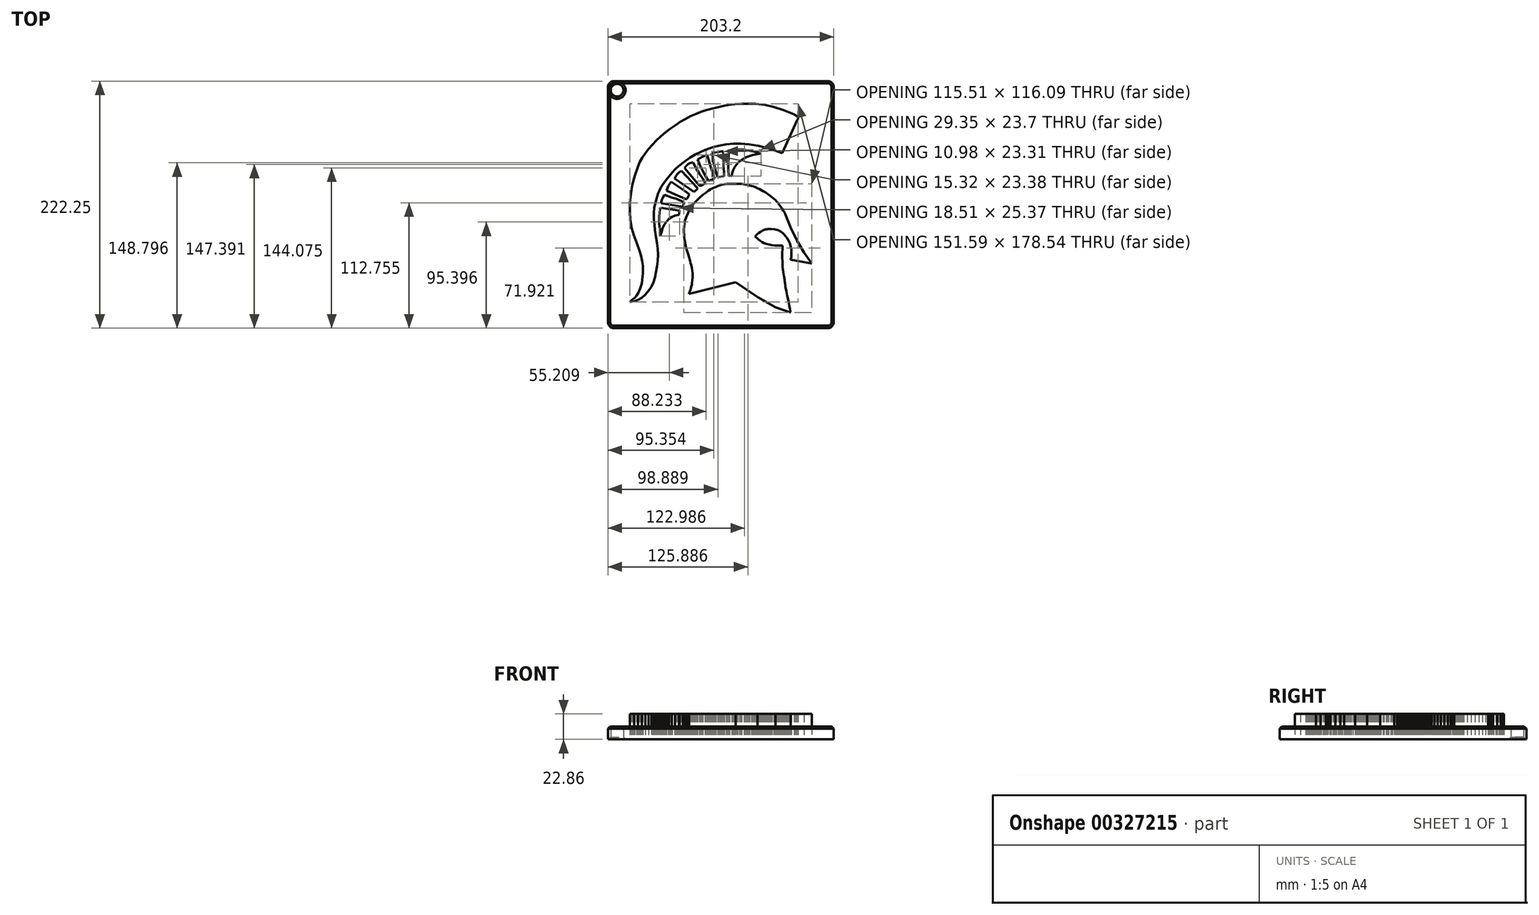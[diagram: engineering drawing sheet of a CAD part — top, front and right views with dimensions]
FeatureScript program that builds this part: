
annotation { "Feature Type Name" : "Feature", "Feature Type Description" : "" }
export const myFeature = defineFeature(function(context is Context, id is Id, definition is map)
    precondition{}
    {
        {
            var Q0;
            Q0=qCreatedBy(makeId("Top.planeOp"),FACE);
            var sketch = newSketch(context, id + "F0", { "sketchPlane" : qUnion([Q0])});
            skLineSegment(sketch, "E0", {"start": v(-81.82, -84.47) * mm, "end": v(-80.11, -82.47) * mm});
            skLineSegment(sketch, "E1", {"start": v(-80.11, -82.47) * mm, "end": v(-79.76, -82.32) * mm});
            skLineSegment(sketch, "E2", {"start": v(-79.76, -82.32) * mm, "end": v(-78.83, -81.76) * mm});
            skLineSegment(sketch, "E3", {"start": v(-78.83, -81.76) * mm, "end": v(-77.48, -80.64) * mm});
            skLineSegment(sketch, "E4", {"start": v(-77.48, -80.64) * mm, "end": v(-75.88, -78.83) * mm});
            skLineSegment(sketch, "E5", {"start": v(-75.88, -78.83) * mm, "end": v(-74.2, -76.16) * mm});
            skLineSegment(sketch, "E6", {"start": v(-74.2, -76.16) * mm, "end": v(-72.61, -72.5) * mm});
            skLineSegment(sketch, "E7", {"start": v(-72.61, -72.5) * mm, "end": v(-71.28, -67.7) * mm});
            skLineSegment(sketch, "E8", {"start": v(-71.28, -67.7) * mm, "end": v(-70.36, -61.6) * mm});
            skLineSegment(sketch, "E9", {"start": v(-70.36, -61.6) * mm, "end": v(-70.11, -58.43) * mm});
            skLineSegment(sketch, "E10", {"start": v(-70.11, -58.43) * mm, "end": v(-70.03, -55.21) * mm});
            skLineSegment(sketch, "E11", {"start": v(-70.03, -55.21) * mm, "end": v(-70.22, -51.75) * mm});
            skLineSegment(sketch, "E12", {"start": v(-70.22, -51.75) * mm, "end": v(-70.77, -47.86) * mm});
            skLineSegment(sketch, "E13", {"start": v(-70.77, -47.86) * mm, "end": v(-71.78, -43.35) * mm});
            skLineSegment(sketch, "E14", {"start": v(-71.78, -43.35) * mm, "end": v(-73.35, -38.02) * mm});
            skLineSegment(sketch, "E15", {"start": v(-73.35, -38.02) * mm, "end": v(-75.57, -31.7) * mm});
            skLineSegment(sketch, "E16", {"start": v(-75.57, -31.7) * mm, "end": v(-78.54, -24.17) * mm});
            skLineSegment(sketch, "E17", {"start": v(-78.54, -24.17) * mm, "end": v(-80.35, -17.68) * mm});
            skLineSegment(sketch, "E18", {"start": v(-80.35, -17.68) * mm, "end": v(-81.52, -10.62) * mm});
            skLineSegment(sketch, "E19", {"start": v(-81.52, -10.62) * mm, "end": v(-82.04, -3.1) * mm});
            skLineSegment(sketch, "E20", {"start": v(-82.04, -3.1) * mm, "end": v(-81.9, 4.77) * mm});
            skLineSegment(sketch, "E21", {"start": v(-81.9, 4.77) * mm, "end": v(-81.12, 12.88) * mm});
            skLineSegment(sketch, "E22", {"start": v(-81.12, 12.88) * mm, "end": v(-79.67, 21.1) * mm});
            skLineSegment(sketch, "E23", {"start": v(-79.67, 21.1) * mm, "end": v(-77.55, 29.32) * mm});
            skLineSegment(sketch, "E24", {"start": v(-77.55, 29.32) * mm, "end": v(-74.76, 37.44) * mm});
            skLineSegment(sketch, "E25", {"start": v(-74.76, 37.44) * mm, "end": v(-72.96, 41.45) * mm});
            skLineSegment(sketch, "E26", {"start": v(-72.96, 41.45) * mm, "end": v(-70.71, 45.46) * mm});
            skLineSegment(sketch, "E27", {"start": v(-70.71, 45.46) * mm, "end": v(-68.05, 49.45) * mm});
            skLineSegment(sketch, "E28", {"start": v(-68.05, 49.45) * mm, "end": v(-65.02, 53.39) * mm});
            skLineSegment(sketch, "E29", {"start": v(-65.02, 53.39) * mm, "end": v(-61.65, 57.26) * mm});
            skLineSegment(sketch, "E30", {"start": v(-61.65, 57.26) * mm, "end": v(-57.99, 61.03) * mm});
            skLineSegment(sketch, "E31", {"start": v(-57.99, 61.03) * mm, "end": v(-54.06, 64.68) * mm});
            skLineSegment(sketch, "E32", {"start": v(-54.06, 64.68) * mm, "end": v(-49.92, 68.19) * mm});
            skLineSegment(sketch, "E33", {"start": v(-49.92, 68.19) * mm, "end": v(-45.6, 71.53) * mm});
            skLineSegment(sketch, "E34", {"start": v(-45.6, 71.53) * mm, "end": v(-41.12, 74.68) * mm});
            skLineSegment(sketch, "E35", {"start": v(-41.12, 74.68) * mm, "end": v(-36.55, 77.6) * mm});
            skLineSegment(sketch, "E36", {"start": v(-36.55, 77.6) * mm, "end": v(-31.9, 80.3) * mm});
            skLineSegment(sketch, "E37", {"start": v(-31.9, 80.3) * mm, "end": v(-27.23, 82.72) * mm});
            skLineSegment(sketch, "E38", {"start": v(-27.23, 82.72) * mm, "end": v(-22.57, 84.86) * mm});
            skLineSegment(sketch, "E39", {"start": v(-22.57, 84.86) * mm, "end": v(-17.96, 86.68) * mm});
            skLineSegment(sketch, "E40", {"start": v(-17.96, 86.68) * mm, "end": v(-13.43, 88.16) * mm});
            skLineSegment(sketch, "E41", {"start": v(-13.43, 88.16) * mm, "end": v(-8.18, 89.63) * mm});
            skLineSegment(sketch, "E42", {"start": v(-8.18, 89.63) * mm, "end": v(-3.03, 90.91) * mm});
            skLineSegment(sketch, "E43", {"start": v(-3.03, 90.91) * mm, "end": v(2.11, 92) * mm});
            skLineSegment(sketch, "E44", {"start": v(2.11, 92) * mm, "end": v(7.35, 92.87) * mm});
            skLineSegment(sketch, "E45", {"start": v(7.35, 92.87) * mm, "end": v(12.8, 93.51) * mm});
            skLineSegment(sketch, "E46", {"start": v(12.8, 93.51) * mm, "end": v(18.53, 93.92) * mm});
            skLineSegment(sketch, "E47", {"start": v(18.53, 93.92) * mm, "end": v(24.67, 94.08) * mm});
            skLineSegment(sketch, "E48", {"start": v(24.67, 94.08) * mm, "end": v(31.31, 93.97) * mm});
            skLineSegment(sketch, "E49", {"start": v(31.31, 93.97) * mm, "end": v(39.54, 93.1) * mm});
            skLineSegment(sketch, "E50", {"start": v(39.54, 93.1) * mm, "end": v(47.72, 91.15) * mm});
            skLineSegment(sketch, "E51", {"start": v(47.72, 91.15) * mm, "end": v(56.34, 88.2) * mm});
            skLineSegment(sketch, "E52", {"start": v(56.34, 88.2) * mm, "end": v(65.9, 84.32) * mm});
            skLineSegment(sketch, "E53", {"start": v(65.9, 84.32) * mm, "end": v(66.02, 84.26) * mm});
            skLineSegment(sketch, "E54", {"start": v(66.02, 84.26) * mm, "end": v(66.35, 84.09) * mm});
            skLineSegment(sketch, "E55", {"start": v(66.35, 84.09) * mm, "end": v(66.82, 83.84) * mm});
            skLineSegment(sketch, "E56", {"start": v(66.82, 83.84) * mm, "end": v(67.38, 83.52) * mm});
            skLineSegment(sketch, "E57", {"start": v(67.38, 83.52) * mm, "end": v(67.97, 83.16) * mm});
            skLineSegment(sketch, "E58", {"start": v(67.97, 83.16) * mm, "end": v(68.54, 82.77) * mm});
            skLineSegment(sketch, "E59", {"start": v(68.54, 82.77) * mm, "end": v(69.01, 82.39) * mm});
            skLineSegment(sketch, "E60", {"start": v(69.01, 82.39) * mm, "end": v(69.34, 82.02) * mm});
            skLineSegment(sketch, "E61", {"start": v(69.34, 82.02) * mm, "end": v(69.55, 81.28) * mm});
            skLineSegment(sketch, "E62", {"start": v(69.55, 81.28) * mm, "end": v(69.37, 80.54) * mm});
            skLineSegment(sketch, "E63", {"start": v(69.37, 80.54) * mm, "end": v(69.07, 79.97) * mm});
            skLineSegment(sketch, "E64", {"start": v(69.07, 79.97) * mm, "end": v(68.92, 79.74) * mm});
            skLineSegment(sketch, "E65", {"start": v(68.92, 79.74) * mm, "end": v(55.1, 49.38) * mm});
            skLineSegment(sketch, "E66", {"start": v(55.1, 49.38) * mm, "end": v(48.24, 52.04) * mm});
            skLineSegment(sketch, "E67", {"start": v(48.24, 52.04) * mm, "end": v(41.22, 54.4) * mm});
            skLineSegment(sketch, "E68", {"start": v(41.22, 54.4) * mm, "end": v(33.72, 56.27) * mm});
            skLineSegment(sketch, "E69", {"start": v(33.72, 56.27) * mm, "end": v(25.43, 57.47) * mm});
            skLineSegment(sketch, "E70", {"start": v(25.43, 57.47) * mm, "end": v(18.16, 57.96) * mm});
            skLineSegment(sketch, "E71", {"start": v(18.16, 57.96) * mm, "end": v(11.43, 57.98) * mm});
            skLineSegment(sketch, "E72", {"start": v(11.43, 57.98) * mm, "end": v(4.83, 57.42) * mm});
            skLineSegment(sketch, "E73", {"start": v(4.83, 57.42) * mm, "end": v(-2.08, 56.17) * mm});
            skLineSegment(sketch, "E74", {"start": v(-2.08, 56.17) * mm, "end": v(-5.93, 55.2) * mm});
            skLineSegment(sketch, "E75", {"start": v(-5.93, 55.2) * mm, "end": v(-9.96, 53.98) * mm});
            skLineSegment(sketch, "E76", {"start": v(-9.96, 53.98) * mm, "end": v(-14.18, 52.43) * mm});
            skLineSegment(sketch, "E77", {"start": v(-14.18, 52.43) * mm, "end": v(-18.58, 50.5) * mm});
            skLineSegment(sketch, "E78", {"start": v(-18.58, 50.5) * mm, "end": v(-23.16, 48.14) * mm});
            skLineSegment(sketch, "E79", {"start": v(-23.16, 48.14) * mm, "end": v(-27.92, 45.3) * mm});
            skLineSegment(sketch, "E80", {"start": v(-27.92, 45.3) * mm, "end": v(-32.85, 41.88) * mm});
            skLineSegment(sketch, "E81", {"start": v(-32.85, 41.88) * mm, "end": v(-37.97, 37.87) * mm});
            skLineSegment(sketch, "E82", {"start": v(-37.97, 37.87) * mm, "end": v(-40.92, 35.16) * mm});
            skLineSegment(sketch, "E83", {"start": v(-40.92, 35.16) * mm, "end": v(-43.9, 32) * mm});
            skLineSegment(sketch, "E84", {"start": v(-43.9, 32) * mm, "end": v(-46.82, 28.56) * mm});
            skLineSegment(sketch, "E85", {"start": v(-46.82, 28.56) * mm, "end": v(-49.52, 25.05) * mm});
            skLineSegment(sketch, "E86", {"start": v(-49.52, 25.05) * mm, "end": v(-51.92, 21.65) * mm});
            skLineSegment(sketch, "E87", {"start": v(-51.92, 21.65) * mm, "end": v(-53.9, 18.55) * mm});
            skLineSegment(sketch, "E88", {"start": v(-53.9, 18.55) * mm, "end": v(-55.32, 15.94) * mm});
            skLineSegment(sketch, "E89", {"start": v(-55.32, 15.94) * mm, "end": v(-56.1, 14) * mm});
            skLineSegment(sketch, "E90", {"start": v(-56.1, 14) * mm, "end": v(-56.4, 13.21) * mm});
            skLineSegment(sketch, "E91", {"start": v(-56.4, 13.21) * mm, "end": v(-57.17, 11.04) * mm});
            skLineSegment(sketch, "E92", {"start": v(-57.17, 11.04) * mm, "end": v(-58.17, 7.82) * mm});
            skLineSegment(sketch, "E93", {"start": v(-58.17, 7.82) * mm, "end": v(-59.22, 3.9) * mm});
            skLineSegment(sketch, "E94", {"start": v(-59.22, 3.9) * mm, "end": v(-59.9, 0.65) * mm});
            skLineSegment(sketch, "E95", {"start": v(-59.9, 0.65) * mm, "end": v(-60.33, -4.33) * mm});
            skLineSegment(sketch, "E96", {"start": v(-60.33, -4.33) * mm, "end": v(-60.2, -9.72) * mm});
            skLineSegment(sketch, "E97", {"start": v(-60.2, -9.72) * mm, "end": v(-59.8, -15.07) * mm});
            skLineSegment(sketch, "E98", {"start": v(-59.8, -15.07) * mm, "end": v(-59.47, -19.88) * mm});
            skLineSegment(sketch, "E99", {"start": v(-59.47, -19.88) * mm, "end": v(-58.37, -26.08) * mm});
            skLineSegment(sketch, "E100", {"start": v(-58.37, -26.08) * mm, "end": v(-57.47, -31.55) * mm});
            skLineSegment(sketch, "E101", {"start": v(-57.47, -31.55) * mm, "end": v(-56.84, -36.7) * mm});
            skLineSegment(sketch, "E102", {"start": v(-56.84, -36.7) * mm, "end": v(-56.58, -41.88) * mm});
            skLineSegment(sketch, "E103", {"start": v(-56.58, -41.88) * mm, "end": v(-56.78, -47.2) * mm});
            skLineSegment(sketch, "E104", {"start": v(-56.78, -47.2) * mm, "end": v(-57.38, -52.46) * mm});
            skLineSegment(sketch, "E105", {"start": v(-57.38, -52.46) * mm, "end": v(-58.28, -57.61) * mm});
            skLineSegment(sketch, "E106", {"start": v(-58.28, -57.61) * mm, "end": v(-59.36, -62.55) * mm});
            skLineSegment(sketch, "E107", {"start": v(-59.36, -62.55) * mm, "end": v(-60.7, -66.75) * mm});
            skLineSegment(sketch, "E108", {"start": v(-60.7, -66.75) * mm, "end": v(-62.66, -70.77) * mm});
            skLineSegment(sketch, "E109", {"start": v(-62.66, -70.77) * mm, "end": v(-65.13, -74.48) * mm});
            skLineSegment(sketch, "E110", {"start": v(-65.13, -74.48) * mm, "end": v(-68.03, -77.78) * mm});
            skLineSegment(sketch, "E111", {"start": v(-68.03, -77.78) * mm, "end": v(-71.24, -80.55) * mm});
            skLineSegment(sketch, "E112", {"start": v(-71.24, -80.55) * mm, "end": v(-74.68, -82.66) * mm});
            skLineSegment(sketch, "E113", {"start": v(-74.68, -82.66) * mm, "end": v(-78.24, -84) * mm});
            skLineSegment(sketch, "E114", {"start": v(-78.24, -84) * mm, "end": v(-81.82, -84.47) * mm});
            skLineSegment(sketch, "E115", {"start": v(-54.53, -25.24) * mm, "end": v(-55.07, -19.51) * mm});
            skLineSegment(sketch, "E116", {"start": v(-55.07, -19.51) * mm, "end": v(-55.59, -13.77) * mm});
            skLineSegment(sketch, "E117", {"start": v(-55.59, -13.77) * mm, "end": v(-55.65, -7.67) * mm});
            skLineSegment(sketch, "E118", {"start": v(-55.65, -7.67) * mm, "end": v(-54.81, -0.87) * mm});
            skLineSegment(sketch, "E119", {"start": v(-54.81, -0.87) * mm, "end": v(-53.88, 0.13) * mm});
            skLineSegment(sketch, "E120", {"start": v(-53.88, 0.13) * mm, "end": v(-37.13, -2.22) * mm});
            skLineSegment(sketch, "E121", {"start": v(-37.13, -2.22) * mm, "end": v(-37.85, -6.21) * mm});
            skLineSegment(sketch, "E122", {"start": v(-37.85, -6.21) * mm, "end": v(-41.3, -6.74) * mm});
            skLineSegment(sketch, "E123", {"start": v(-41.3, -6.74) * mm, "end": v(-44.26, -7.92) * mm});
            skLineSegment(sketch, "E124", {"start": v(-44.26, -7.92) * mm, "end": v(-46.8, -9.68) * mm});
            skLineSegment(sketch, "E125", {"start": v(-46.8, -9.68) * mm, "end": v(-48.95, -11.97) * mm});
            skLineSegment(sketch, "E126", {"start": v(-48.95, -11.97) * mm, "end": v(-50.75, -14.73) * mm});
            skLineSegment(sketch, "E127", {"start": v(-50.75, -14.73) * mm, "end": v(-52.26, -17.9) * mm});
            skLineSegment(sketch, "E128", {"start": v(-52.26, -17.9) * mm, "end": v(-53.5, -21.42) * mm});
            skLineSegment(sketch, "E129", {"start": v(-53.5, -21.42) * mm, "end": v(-54.53, -25.24) * mm});
            skLineSegment(sketch, "E130", {"start": v(-28.63, -77.13) * mm, "end": v(-28.54, -76.85) * mm});
            skLineSegment(sketch, "E131", {"start": v(-28.54, -76.85) * mm, "end": v(-28.29, -76.07) * mm});
            skLineSegment(sketch, "E132", {"start": v(-28.29, -76.07) * mm, "end": v(-27.92, -74.93) * mm});
            skLineSegment(sketch, "E133", {"start": v(-27.92, -74.93) * mm, "end": v(-27.48, -73.52) * mm});
            skLineSegment(sketch, "E134", {"start": v(-27.48, -73.52) * mm, "end": v(-27.02, -71.97) * mm});
            skLineSegment(sketch, "E135", {"start": v(-27.02, -71.97) * mm, "end": v(-26.57, -70.4) * mm});
            skLineSegment(sketch, "E136", {"start": v(-26.57, -70.4) * mm, "end": v(-26.18, -68.9) * mm});
            skLineSegment(sketch, "E137", {"start": v(-26.18, -68.9) * mm, "end": v(-25.9, -67.6) * mm});
            skLineSegment(sketch, "E138", {"start": v(-25.9, -67.6) * mm, "end": v(-25.58, -64.97) * mm});
            skLineSegment(sketch, "E139", {"start": v(-25.58, -64.97) * mm, "end": v(-25.44, -62.18) * mm});
            skLineSegment(sketch, "E140", {"start": v(-25.44, -62.18) * mm, "end": v(-25.4, -59.98) * mm});
            skLineSegment(sketch, "E141", {"start": v(-25.4, -59.98) * mm, "end": v(-25.4, -59.09) * mm});
            skLineSegment(sketch, "E142", {"start": v(-25.4, -59.09) * mm, "end": v(-25.5, -58.38) * mm});
            skLineSegment(sketch, "E143", {"start": v(-25.5, -58.38) * mm, "end": v(-25.75, -56.56) * mm});
            skLineSegment(sketch, "E144", {"start": v(-25.75, -56.56) * mm, "end": v(-26.19, -54.03) * mm});
            skLineSegment(sketch, "E145", {"start": v(-26.19, -54.03) * mm, "end": v(-26.82, -51.22) * mm});
            skLineSegment(sketch, "E146", {"start": v(-26.82, -51.22) * mm, "end": v(-27.25, -49.6) * mm});
            skLineSegment(sketch, "E147", {"start": v(-27.25, -49.6) * mm, "end": v(-27.8, -47.67) * mm});
            skLineSegment(sketch, "E148", {"start": v(-27.8, -47.67) * mm, "end": v(-28.42, -45.53) * mm});
            skLineSegment(sketch, "E149", {"start": v(-28.42, -45.53) * mm, "end": v(-29.06, -43.3) * mm});
            skLineSegment(sketch, "E150", {"start": v(-29.06, -43.3) * mm, "end": v(-29.69, -41.13) * mm});
            skLineSegment(sketch, "E151", {"start": v(-29.69, -41.13) * mm, "end": v(-30.25, -39.11) * mm});
            skLineSegment(sketch, "E152", {"start": v(-30.25, -39.11) * mm, "end": v(-30.71, -37.4) * mm});
            skLineSegment(sketch, "E153", {"start": v(-30.71, -37.4) * mm, "end": v(-31.02, -36.08) * mm});
            skLineSegment(sketch, "E154", {"start": v(-31.02, -36.08) * mm, "end": v(-31.67, -33.63) * mm});
            skLineSegment(sketch, "E155", {"start": v(-31.67, -33.63) * mm, "end": v(-32.2, -30.97) * mm});
            skLineSegment(sketch, "E156", {"start": v(-32.2, -30.97) * mm, "end": v(-32.63, -28.27) * mm});
            skLineSegment(sketch, "E157", {"start": v(-32.63, -28.27) * mm, "end": v(-32.95, -25.69) * mm});
            skLineSegment(sketch, "E158", {"start": v(-32.95, -25.69) * mm, "end": v(-33.2, -23.4) * mm});
            skLineSegment(sketch, "E159", {"start": v(-33.2, -23.4) * mm, "end": v(-33.35, -21.55) * mm});
            skLineSegment(sketch, "E160", {"start": v(-33.35, -21.55) * mm, "end": v(-33.44, -20.32) * mm});
            skLineSegment(sketch, "E161", {"start": v(-33.44, -20.32) * mm, "end": v(-33.47, -19.88) * mm});
            skLineSegment(sketch, "E162", {"start": v(-33.47, -19.88) * mm, "end": v(-33.4, -18.95) * mm});
            skLineSegment(sketch, "E163", {"start": v(-33.4, -18.95) * mm, "end": v(-33.16, -16.7) * mm});
            skLineSegment(sketch, "E164", {"start": v(-33.16, -16.7) * mm, "end": v(-32.78, -13.95) * mm});
            skLineSegment(sketch, "E165", {"start": v(-32.78, -13.95) * mm, "end": v(-32.25, -11.5) * mm});
            skLineSegment(sketch, "E166", {"start": v(-32.25, -11.5) * mm, "end": v(-31.06, -7.95) * mm});
            skLineSegment(sketch, "E167", {"start": v(-31.06, -7.95) * mm, "end": v(-29.6, -4.42) * mm});
            skLineSegment(sketch, "E168", {"start": v(-29.6, -4.42) * mm, "end": v(-27.95, -1.1) * mm});
            skLineSegment(sketch, "E169", {"start": v(-27.95, -1.1) * mm, "end": v(-26.22, 1.82) * mm});
            skLineSegment(sketch, "E170", {"start": v(-26.22, 1.82) * mm, "end": v(-24.28, 4.32) * mm});
            skLineSegment(sketch, "E171", {"start": v(-24.28, 4.32) * mm, "end": v(-21.77, 6.93) * mm});
            skLineSegment(sketch, "E172", {"start": v(-21.77, 6.93) * mm, "end": v(-18.95, 9.51) * mm});
            skLineSegment(sketch, "E173", {"start": v(-18.95, 9.51) * mm, "end": v(-16.07, 11.92) * mm});
            skLineSegment(sketch, "E174", {"start": v(-16.07, 11.92) * mm, "end": v(-13.4, 14.04) * mm});
            skLineSegment(sketch, "E175", {"start": v(-13.4, 14.04) * mm, "end": v(-11.17, 15.71) * mm});
            skLineSegment(sketch, "E176", {"start": v(-11.17, 15.71) * mm, "end": v(-9.64, 16.82) * mm});
            skLineSegment(sketch, "E177", {"start": v(-9.64, 16.82) * mm, "end": v(-9.08, 17.21) * mm});
            skLineSegment(sketch, "E178", {"start": v(-9.08, 17.21) * mm, "end": v(-8.73, 17.37) * mm});
            skLineSegment(sketch, "E179", {"start": v(-8.73, 17.37) * mm, "end": v(-7.79, 17.78) * mm});
            skLineSegment(sketch, "E180", {"start": v(-7.79, 17.78) * mm, "end": v(-6.36, 18.37) * mm});
            skLineSegment(sketch, "E181", {"start": v(-6.36, 18.37) * mm, "end": v(-4.6, 19.08) * mm});
            skLineSegment(sketch, "E182", {"start": v(-4.6, 19.08) * mm, "end": v(-2.63, 19.82) * mm});
            skLineSegment(sketch, "E183", {"start": v(-2.63, 19.82) * mm, "end": v(-0.57, 20.54) * mm});
            skLineSegment(sketch, "E184", {"start": v(-0.57, 20.54) * mm, "end": v(1.43, 21.14) * mm});
            skLineSegment(sketch, "E185", {"start": v(1.43, 21.14) * mm, "end": v(3.26, 21.57) * mm});
            skLineSegment(sketch, "E186", {"start": v(3.26, 21.57) * mm, "end": v(5.53, 21.8) * mm});
            skLineSegment(sketch, "E187", {"start": v(5.53, 21.8) * mm, "end": v(7.95, 21.93) * mm});
            skLineSegment(sketch, "E188", {"start": v(7.95, 21.93) * mm, "end": v(10.39, 22) * mm});
            skLineSegment(sketch, "E189", {"start": v(10.39, 22) * mm, "end": v(12.7, 22.02) * mm});
            skLineSegment(sketch, "E190", {"start": v(12.7, 22.02) * mm, "end": v(14.74, 22) * mm});
            skLineSegment(sketch, "E191", {"start": v(14.74, 22) * mm, "end": v(16.37, 21.98) * mm});
            skLineSegment(sketch, "E192", {"start": v(16.37, 21.98) * mm, "end": v(17.45, 21.96) * mm});
            skLineSegment(sketch, "E193", {"start": v(17.45, 21.96) * mm, "end": v(17.84, 21.95) * mm});
            skLineSegment(sketch, "E194", {"start": v(17.84, 21.95) * mm, "end": v(18.18, 21.9) * mm});
            skLineSegment(sketch, "E195", {"start": v(18.18, 21.9) * mm, "end": v(19.13, 21.74) * mm});
            skLineSegment(sketch, "E196", {"start": v(19.13, 21.74) * mm, "end": v(20.53, 21.5) * mm});
            skLineSegment(sketch, "E197", {"start": v(20.53, 21.5) * mm, "end": v(22.23, 21.19) * mm});
            skLineSegment(sketch, "E198", {"start": v(22.23, 21.19) * mm, "end": v(24.1, 20.82) * mm});
            skLineSegment(sketch, "E199", {"start": v(24.1, 20.82) * mm, "end": v(25.96, 20.43) * mm});
            skLineSegment(sketch, "E200", {"start": v(25.96, 20.43) * mm, "end": v(27.69, 20.01) * mm});
            skLineSegment(sketch, "E201", {"start": v(27.69, 20.01) * mm, "end": v(29.13, 19.6) * mm});
            skLineSegment(sketch, "E202", {"start": v(29.13, 19.6) * mm, "end": v(30.92, 18.92) * mm});
            skLineSegment(sketch, "E203", {"start": v(30.92, 18.92) * mm, "end": v(32.84, 18.06) * mm});
            skLineSegment(sketch, "E204", {"start": v(32.84, 18.06) * mm, "end": v(34.77, 17.1) * mm});
            skLineSegment(sketch, "E205", {"start": v(34.77, 17.1) * mm, "end": v(36.61, 16.13) * mm});
            skLineSegment(sketch, "E206", {"start": v(36.61, 16.13) * mm, "end": v(38.24, 15.23) * mm});
            skLineSegment(sketch, "E207", {"start": v(38.24, 15.23) * mm, "end": v(39.54, 14.48) * mm});
            skLineSegment(sketch, "E208", {"start": v(39.54, 14.48) * mm, "end": v(40.4, 13.97) * mm});
            skLineSegment(sketch, "E209", {"start": v(40.4, 13.97) * mm, "end": v(40.71, 13.79) * mm});
            skLineSegment(sketch, "E210", {"start": v(40.71, 13.79) * mm, "end": v(41.01, 13.57) * mm});
            skLineSegment(sketch, "E211", {"start": v(41.01, 13.57) * mm, "end": v(41.82, 12.99) * mm});
            skLineSegment(sketch, "E212", {"start": v(41.82, 12.99) * mm, "end": v(43, 12.1) * mm});
            skLineSegment(sketch, "E213", {"start": v(43, 12.1) * mm, "end": v(44.45, 11) * mm});
            skLineSegment(sketch, "E214", {"start": v(44.45, 11) * mm, "end": v(46.03, 9.75) * mm});
            skLineSegment(sketch, "E215", {"start": v(46.03, 9.75) * mm, "end": v(47.62, 8.44) * mm});
            skLineSegment(sketch, "E216", {"start": v(47.62, 8.44) * mm, "end": v(49.08, 7.15) * mm});
            skLineSegment(sketch, "E217", {"start": v(49.08, 7.15) * mm, "end": v(50.3, 5.94) * mm});
            skLineSegment(sketch, "E218", {"start": v(50.3, 5.94) * mm, "end": v(51.48, 4.57) * mm});
            skLineSegment(sketch, "E219", {"start": v(51.48, 4.57) * mm, "end": v(52.74, 2.92) * mm});
            skLineSegment(sketch, "E220", {"start": v(52.74, 2.92) * mm, "end": v(54, 1.15) * mm});
            skLineSegment(sketch, "E221", {"start": v(54, 1.15) * mm, "end": v(55.2, -0.6) * mm});
            skLineSegment(sketch, "E222", {"start": v(55.2, -0.6) * mm, "end": v(56.24, -2.21) * mm});
            skLineSegment(sketch, "E223", {"start": v(56.24, -2.21) * mm, "end": v(57.09, -3.54) * mm});
            skLineSegment(sketch, "E224", {"start": v(57.09, -3.54) * mm, "end": v(57.65, -4.43) * mm});
            skLineSegment(sketch, "E225", {"start": v(57.65, -4.43) * mm, "end": v(57.85, -4.76) * mm});
            skLineSegment(sketch, "E226", {"start": v(57.85, -4.76) * mm, "end": v(62.78, -17.36) * mm});
            skLineSegment(sketch, "E227", {"start": v(62.78, -17.36) * mm, "end": v(68.43, -29.1) * mm});
            skLineSegment(sketch, "E228", {"start": v(68.43, -29.1) * mm, "end": v(74.84, -39.93) * mm});
            skLineSegment(sketch, "E229", {"start": v(74.84, -39.93) * mm, "end": v(82.04, -49.81) * mm});
            skLineSegment(sketch, "E230", {"start": v(82.04, -49.81) * mm, "end": v(62.89, -46.29) * mm});
            skLineSegment(sketch, "E231", {"start": v(62.89, -46.29) * mm, "end": v(62.97, -45.98) * mm});
            skLineSegment(sketch, "E232", {"start": v(62.97, -45.98) * mm, "end": v(63.16, -45.1) * mm});
            skLineSegment(sketch, "E233", {"start": v(63.16, -45.1) * mm, "end": v(63.38, -43.74) * mm});
            skLineSegment(sketch, "E234", {"start": v(63.38, -43.74) * mm, "end": v(63.55, -41.94) * mm});
            skLineSegment(sketch, "E235", {"start": v(63.55, -41.94) * mm, "end": v(63.6, -39.79) * mm});
            skLineSegment(sketch, "E236", {"start": v(63.6, -39.79) * mm, "end": v(63.43, -37.34) * mm});
            skLineSegment(sketch, "E237", {"start": v(63.43, -37.34) * mm, "end": v(63, -34.68) * mm});
            skLineSegment(sketch, "E238", {"start": v(63, -34.68) * mm, "end": v(62.2, -31.86) * mm});
            skLineSegment(sketch, "E239", {"start": v(62.2, -31.86) * mm, "end": v(61.05, -29.23) * mm});
            skLineSegment(sketch, "E240", {"start": v(61.05, -29.23) * mm, "end": v(59.7, -26.95) * mm});
            skLineSegment(sketch, "E241", {"start": v(59.7, -26.95) * mm, "end": v(58.23, -25.03) * mm});
            skLineSegment(sketch, "E242", {"start": v(58.23, -25.03) * mm, "end": v(56.77, -23.46) * mm});
            skLineSegment(sketch, "E243", {"start": v(56.77, -23.46) * mm, "end": v(55.43, -22.24) * mm});
            skLineSegment(sketch, "E244", {"start": v(55.43, -22.24) * mm, "end": v(54.33, -21.38) * mm});
            skLineSegment(sketch, "E245", {"start": v(54.33, -21.38) * mm, "end": v(53.59, -20.86) * mm});
            skLineSegment(sketch, "E246", {"start": v(53.59, -20.86) * mm, "end": v(53.31, -20.69) * mm});
            skLineSegment(sketch, "E247", {"start": v(53.31, -20.69) * mm, "end": v(52.71, -20.39) * mm});
            skLineSegment(sketch, "E248", {"start": v(52.71, -20.39) * mm, "end": v(51.03, -19.73) * mm});
            skLineSegment(sketch, "E249", {"start": v(51.03, -19.73) * mm, "end": v(48.48, -19.05) * mm});
            skLineSegment(sketch, "E250", {"start": v(48.48, -19.05) * mm, "end": v(45.26, -18.71) * mm});
            skLineSegment(sketch, "E251", {"start": v(45.26, -18.71) * mm, "end": v(44.61, -18.72) * mm});
            skLineSegment(sketch, "E252", {"start": v(44.61, -18.72) * mm, "end": v(43.86, -18.77) * mm});
            skLineSegment(sketch, "E253", {"start": v(43.86, -18.77) * mm, "end": v(43.05, -18.83) * mm});
            skLineSegment(sketch, "E254", {"start": v(43.05, -18.83) * mm, "end": v(42.25, -18.91) * mm});
            skLineSegment(sketch, "E255", {"start": v(42.25, -18.91) * mm, "end": v(41.52, -18.99) * mm});
            skLineSegment(sketch, "E256", {"start": v(41.52, -18.99) * mm, "end": v(40.92, -19.06) * mm});
            skLineSegment(sketch, "E257", {"start": v(40.92, -19.06) * mm, "end": v(40.51, -19.1) * mm});
            skLineSegment(sketch, "E258", {"start": v(40.51, -19.1) * mm, "end": v(40.37, -19.13) * mm});
            skLineSegment(sketch, "E259", {"start": v(40.37, -19.13) * mm, "end": v(37.89, -20.17) * mm});
            skLineSegment(sketch, "E260", {"start": v(37.89, -20.17) * mm, "end": v(35.84, -21.26) * mm});
            skLineSegment(sketch, "E261", {"start": v(35.84, -21.26) * mm, "end": v(34.18, -22.33) * mm});
            skLineSegment(sketch, "E262", {"start": v(34.18, -22.33) * mm, "end": v(32.9, -23.33) * mm});
            skLineSegment(sketch, "E263", {"start": v(32.9, -23.33) * mm, "end": v(31.94, -24.2) * mm});
            skLineSegment(sketch, "E264", {"start": v(31.94, -24.2) * mm, "end": v(31.3, -24.9) * mm});
            skLineSegment(sketch, "E265", {"start": v(31.3, -24.9) * mm, "end": v(30.94, -25.36) * mm});
            skLineSegment(sketch, "E266", {"start": v(30.94, -25.36) * mm, "end": v(30.82, -25.52) * mm});
            skLineSegment(sketch, "E267", {"start": v(30.82, -25.52) * mm, "end": v(31.05, -25.74) * mm});
            skLineSegment(sketch, "E268", {"start": v(31.05, -25.74) * mm, "end": v(31.67, -26.32) * mm});
            skLineSegment(sketch, "E269", {"start": v(31.67, -26.32) * mm, "end": v(32.64, -27.17) * mm});
            skLineSegment(sketch, "E270", {"start": v(32.64, -27.17) * mm, "end": v(33.9, -28.2) * mm});
            skLineSegment(sketch, "E271", {"start": v(33.9, -28.2) * mm, "end": v(35.38, -29.3) * mm});
            skLineSegment(sketch, "E272", {"start": v(35.38, -29.3) * mm, "end": v(37.03, -30.37) * mm});
            skLineSegment(sketch, "E273", {"start": v(37.03, -30.37) * mm, "end": v(38.79, -31.33) * mm});
            skLineSegment(sketch, "E274", {"start": v(38.79, -31.33) * mm, "end": v(40.6, -32.08) * mm});
            skLineSegment(sketch, "E275", {"start": v(40.6, -32.08) * mm, "end": v(43.43, -32.87) * mm});
            skLineSegment(sketch, "E276", {"start": v(43.43, -32.87) * mm, "end": v(46.16, -33.4) * mm});
            skLineSegment(sketch, "E277", {"start": v(46.16, -33.4) * mm, "end": v(48.7, -33.7) * mm});
            skLineSegment(sketch, "E278", {"start": v(48.7, -33.7) * mm, "end": v(50.97, -33.83) * mm});
            skLineSegment(sketch, "E279", {"start": v(50.97, -33.83) * mm, "end": v(52.88, -33.85) * mm});
            skLineSegment(sketch, "E280", {"start": v(52.88, -33.85) * mm, "end": v(54.35, -33.8) * mm});
            skLineSegment(sketch, "E281", {"start": v(54.35, -33.8) * mm, "end": v(55.3, -33.72) * mm});
            skLineSegment(sketch, "E282", {"start": v(55.3, -33.72) * mm, "end": v(55.63, -33.69) * mm});
            skLineSegment(sketch, "E283", {"start": v(55.63, -33.69) * mm, "end": v(55.59, -34.5) * mm});
            skLineSegment(sketch, "E284", {"start": v(55.59, -34.5) * mm, "end": v(55.48, -36.71) * mm});
            skLineSegment(sketch, "E285", {"start": v(55.48, -36.71) * mm, "end": v(55.38, -40.01) * mm});
            skLineSegment(sketch, "E286", {"start": v(55.38, -40.01) * mm, "end": v(55.34, -44.07) * mm});
            skLineSegment(sketch, "E287", {"start": v(55.34, -44.07) * mm, "end": v(55.41, -48.56) * mm});
            skLineSegment(sketch, "E288", {"start": v(55.41, -48.56) * mm, "end": v(55.65, -53.17) * mm});
            skLineSegment(sketch, "E289", {"start": v(55.65, -53.17) * mm, "end": v(56.13, -57.56) * mm});
            skLineSegment(sketch, "E290", {"start": v(56.13, -57.56) * mm, "end": v(56.89, -61.42) * mm});
            skLineSegment(sketch, "E291", {"start": v(56.89, -61.42) * mm, "end": v(57.04, -62.2) * mm});
            skLineSegment(sketch, "E292", {"start": v(57.04, -62.2) * mm, "end": v(57.14, -62.89) * mm});
            skLineSegment(sketch, "E293", {"start": v(57.14, -62.89) * mm, "end": v(57.32, -64.36) * mm});
            skLineSegment(sketch, "E294", {"start": v(57.32, -64.36) * mm, "end": v(57.42, -65.36) * mm});
            skLineSegment(sketch, "E295", {"start": v(57.42, -65.36) * mm, "end": v(57.48, -65.83) * mm});
            skLineSegment(sketch, "E296", {"start": v(57.48, -65.83) * mm, "end": v(57.53, -66.17) * mm});
            skLineSegment(sketch, "E297", {"start": v(57.53, -66.17) * mm, "end": v(57.6, -66.74) * mm});
            skLineSegment(sketch, "E298", {"start": v(57.6, -66.74) * mm, "end": v(58.17, -70.86) * mm});
            skLineSegment(sketch, "E299", {"start": v(58.17, -70.86) * mm, "end": v(58.97, -75.1) * mm});
            skLineSegment(sketch, "E300", {"start": v(58.97, -75.1) * mm, "end": v(59.76, -78.71) * mm});
            skLineSegment(sketch, "E301", {"start": v(59.76, -78.71) * mm, "end": v(60.48, -82.18) * mm});
            skLineSegment(sketch, "E302", {"start": v(60.48, -82.18) * mm, "end": v(61.12, -85.4) * mm});
            skLineSegment(sketch, "E303", {"start": v(61.12, -85.4) * mm, "end": v(61.68, -88.25) * mm});
            skLineSegment(sketch, "E304", {"start": v(61.68, -88.25) * mm, "end": v(62.13, -90.64) * mm});
            skLineSegment(sketch, "E305", {"start": v(62.13, -90.64) * mm, "end": v(62.47, -92.48) * mm});
            skLineSegment(sketch, "E306", {"start": v(62.47, -92.48) * mm, "end": v(62.68, -93.66) * mm});
            skLineSegment(sketch, "E307", {"start": v(62.68, -93.66) * mm, "end": v(62.76, -94.08) * mm});
            skLineSegment(sketch, "E308", {"start": v(62.76, -94.08) * mm, "end": v(49.18, -89.1) * mm});
            skLineSegment(sketch, "E309", {"start": v(49.18, -89.1) * mm, "end": v(32.97, -79.9) * mm});
            skLineSegment(sketch, "E310", {"start": v(32.97, -79.9) * mm, "end": v(13.4, -66.65) * mm});
            skLineSegment(sketch, "E311", {"start": v(13.4, -66.65) * mm, "end": v(-28.63, -77.13) * mm});
            skLineSegment(sketch, "E312", {"start": v(6.91, 29.14) * mm, "end": v(6.77, 34.65) * mm});
            skLineSegment(sketch, "E313", {"start": v(6.77, 34.65) * mm, "end": v(6.71, 40.24) * mm});
            skLineSegment(sketch, "E314", {"start": v(6.71, 40.24) * mm, "end": v(6.86, 46) * mm});
            skLineSegment(sketch, "E315", {"start": v(6.86, 46) * mm, "end": v(7.34, 52.02) * mm});
            skLineSegment(sketch, "E316", {"start": v(7.34, 52.02) * mm, "end": v(12.42, 52.54) * mm});
            skLineSegment(sketch, "E317", {"start": v(12.42, 52.54) * mm, "end": v(16.87, 52.7) * mm});
            skLineSegment(sketch, "E318", {"start": v(16.87, 52.7) * mm, "end": v(20.8, 52.53) * mm});
            skLineSegment(sketch, "E319", {"start": v(20.8, 52.53) * mm, "end": v(24.31, 52.1) * mm});
            skLineSegment(sketch, "E320", {"start": v(24.31, 52.1) * mm, "end": v(27.5, 51.48) * mm});
            skLineSegment(sketch, "E321", {"start": v(27.5, 51.48) * mm, "end": v(30.45, 50.72) * mm});
            skLineSegment(sketch, "E322", {"start": v(30.45, 50.72) * mm, "end": v(33.27, 49.88) * mm});
            skLineSegment(sketch, "E323", {"start": v(33.27, 49.88) * mm, "end": v(36.06, 49.02) * mm});
            skLineSegment(sketch, "E324", {"start": v(36.06, 49.02) * mm, "end": v(28.88, 47.98) * mm});
            skLineSegment(sketch, "E325", {"start": v(28.88, 47.98) * mm, "end": v(23.1, 46.07) * mm});
            skLineSegment(sketch, "E326", {"start": v(23.1, 46.07) * mm, "end": v(18.6, 43.53) * mm});
            skLineSegment(sketch, "E327", {"start": v(18.6, 43.53) * mm, "end": v(15.2, 40.57) * mm});
            skLineSegment(sketch, "E328", {"start": v(15.2, 40.57) * mm, "end": v(12.77, 37.42) * mm});
            skLineSegment(sketch, "E329", {"start": v(12.77, 37.42) * mm, "end": v(11.18, 34.3) * mm});
            skLineSegment(sketch, "E330", {"start": v(11.18, 34.3) * mm, "end": v(10.27, 31.41) * mm});
            skLineSegment(sketch, "E331", {"start": v(10.27, 31.41) * mm, "end": v(9.9, 29) * mm});
            skLineSegment(sketch, "E332", {"start": v(9.9, 29) * mm, "end": v(6.91, 29.14) * mm});
            skLineSegment(sketch, "E333", {"start": v(-8.2, 49.45) * mm, "end": v(-5.31, 50.04) * mm});
            skLineSegment(sketch, "E334", {"start": v(-5.31, 50.04) * mm, "end": v(-2.98, 50.46) * mm});
            skLineSegment(sketch, "E335", {"start": v(-2.98, 50.46) * mm, "end": v(-1.15, 50.75) * mm});
            skLineSegment(sketch, "E336", {"start": v(-1.15, 50.75) * mm, "end": v(0.22, 50.94) * mm});
            skLineSegment(sketch, "E337", {"start": v(0.22, 50.94) * mm, "end": v(1.2, 51.04) * mm});
            skLineSegment(sketch, "E338", {"start": v(1.2, 51.04) * mm, "end": v(1.83, 51.09) * mm});
            skLineSegment(sketch, "E339", {"start": v(1.83, 51.09) * mm, "end": v(2.18, 51.1) * mm});
            skLineSegment(sketch, "E340", {"start": v(2.18, 51.1) * mm, "end": v(2.28, 51.1) * mm});
            skLineSegment(sketch, "E341", {"start": v(2.28, 51.1) * mm, "end": v(2.78, 28.57) * mm});
            skLineSegment(sketch, "E342", {"start": v(2.78, 28.57) * mm, "end": v(-2.78, 27.79) * mm});
            skLineSegment(sketch, "E343", {"start": v(-2.78, 27.79) * mm, "end": v(-4.37, 32.7) * mm});
            skLineSegment(sketch, "E344", {"start": v(-4.37, 32.7) * mm, "end": v(-5.84, 37.85) * mm});
            skLineSegment(sketch, "E345", {"start": v(-5.84, 37.85) * mm, "end": v(-7.14, 43.38) * mm});
            skLineSegment(sketch, "E346", {"start": v(-7.14, 43.38) * mm, "end": v(-8.2, 49.45) * mm});
            skLineSegment(sketch, "E347", {"start": v(-12.47, 47.81) * mm, "end": v(-9.1, 37.44) * mm});
            skLineSegment(sketch, "E348", {"start": v(-9.1, 37.44) * mm, "end": v(-5.7, 26.57) * mm});
            skLineSegment(sketch, "E349", {"start": v(-5.7, 26.57) * mm, "end": v(-10.98, 24.44) * mm});
            skLineSegment(sketch, "E350", {"start": v(-10.98, 24.44) * mm, "end": v(-13.72, 28.65) * mm});
            skLineSegment(sketch, "E351", {"start": v(-13.72, 28.65) * mm, "end": v(-16.29, 33.35) * mm});
            skLineSegment(sketch, "E352", {"start": v(-16.29, 33.35) * mm, "end": v(-18.71, 38.44) * mm});
            skLineSegment(sketch, "E353", {"start": v(-18.71, 38.44) * mm, "end": v(-21.03, 43.82) * mm});
            skLineSegment(sketch, "E354", {"start": v(-21.03, 43.82) * mm, "end": v(-16.68, 46.24) * mm});
            skLineSegment(sketch, "E355", {"start": v(-16.68, 46.24) * mm, "end": v(-12.47, 47.81) * mm});
            skLineSegment(sketch, "E356", {"start": v(-25.02, 41.33) * mm, "end": v(-27.64, 40.71) * mm});
            skLineSegment(sketch, "E357", {"start": v(-27.64, 40.71) * mm, "end": v(-29.63, 39.53) * mm});
            skLineSegment(sketch, "E358", {"start": v(-29.63, 39.53) * mm, "end": v(-31.21, 37.96) * mm});
            skLineSegment(sketch, "E359", {"start": v(-31.21, 37.96) * mm, "end": v(-32.57, 36.2) * mm});
            skLineSegment(sketch, "E360", {"start": v(-32.57, 36.2) * mm, "end": v(-19.25, 20.3) * mm});
            skLineSegment(sketch, "E361", {"start": v(-19.25, 20.3) * mm, "end": v(-18.54, 20.2) * mm});
            skLineSegment(sketch, "E362", {"start": v(-18.54, 20.2) * mm, "end": v(-18.02, 20.17) * mm});
            skLineSegment(sketch, "E363", {"start": v(-18.02, 20.17) * mm, "end": v(-17.6, 20.16) * mm});
            skLineSegment(sketch, "E364", {"start": v(-17.6, 20.16) * mm, "end": v(-17.18, 20.16) * mm});
            skLineSegment(sketch, "E365", {"start": v(-17.18, 20.16) * mm, "end": v(-13.9, 22.51) * mm});
            skLineSegment(sketch, "E366", {"start": v(-13.9, 22.51) * mm, "end": v(-16.63, 26.88) * mm});
            skLineSegment(sketch, "E367", {"start": v(-16.63, 26.88) * mm, "end": v(-19.33, 31.16) * mm});
            skLineSegment(sketch, "E368", {"start": v(-19.33, 31.16) * mm, "end": v(-22.1, 35.82) * mm});
            skLineSegment(sketch, "E369", {"start": v(-22.1, 35.82) * mm, "end": v(-25.02, 41.33) * mm});
            skLineSegment(sketch, "E370", {"start": v(-41.7, 26.72) * mm, "end": v(-40.56, 28.53) * mm});
            skLineSegment(sketch, "E371", {"start": v(-40.56, 28.53) * mm, "end": v(-39.26, 30.31) * mm});
            skLineSegment(sketch, "E372", {"start": v(-39.26, 30.31) * mm, "end": v(-37.65, 32.03) * mm});
            skLineSegment(sketch, "E373", {"start": v(-37.65, 32.03) * mm, "end": v(-35.57, 33.63) * mm});
            skLineSegment(sketch, "E374", {"start": v(-35.57, 33.63) * mm, "end": v(-21.03, 18.02) * mm});
            skLineSegment(sketch, "E375", {"start": v(-21.03, 18.02) * mm, "end": v(-21.7, 16.85) * mm});
            skLineSegment(sketch, "E376", {"start": v(-21.7, 16.85) * mm, "end": v(-22.8, 15.81) * mm});
            skLineSegment(sketch, "E377", {"start": v(-22.8, 15.81) * mm, "end": v(-24.1, 14.53) * mm});
            skLineSegment(sketch, "E378", {"start": v(-24.1, 14.53) * mm, "end": v(-41.7, 26.72) * mm});
            skLineSegment(sketch, "E379", {"start": v(-44.76, 23.65) * mm, "end": v(-47.47, 20.02) * mm});
            skLineSegment(sketch, "E380", {"start": v(-47.47, 20.02) * mm, "end": v(-49.04, 15.95) * mm});
            skLineSegment(sketch, "E381", {"start": v(-49.04, 15.95) * mm, "end": v(-44.05, 13.7) * mm});
            skLineSegment(sketch, "E382", {"start": v(-44.05, 13.7) * mm, "end": v(-39.14, 11.5) * mm});
            skLineSegment(sketch, "E383", {"start": v(-39.14, 11.5) * mm, "end": v(-34.6, 9.52) * mm});
            skLineSegment(sketch, "E384", {"start": v(-34.6, 9.52) * mm, "end": v(-30.72, 7.97) * mm});
            skLineSegment(sketch, "E385", {"start": v(-30.72, 7.97) * mm, "end": v(-30.5, 8.38) * mm});
            skLineSegment(sketch, "E386", {"start": v(-30.5, 8.38) * mm, "end": v(-30.3, 8.74) * mm});
            skLineSegment(sketch, "E387", {"start": v(-30.3, 8.74) * mm, "end": v(-30.1, 9.1) * mm});
            skLineSegment(sketch, "E388", {"start": v(-30.1, 9.1) * mm, "end": v(-29.87, 9.5) * mm});
            skLineSegment(sketch, "E389", {"start": v(-29.87, 9.5) * mm, "end": v(-29.6, 10) * mm});
            skLineSegment(sketch, "E390", {"start": v(-29.6, 10) * mm, "end": v(-29.28, 10.62) * mm});
            skLineSegment(sketch, "E391", {"start": v(-29.28, 10.62) * mm, "end": v(-28.88, 11.43) * mm});
            skLineSegment(sketch, "E392", {"start": v(-28.88, 11.43) * mm, "end": v(-28.37, 12.46) * mm});
            skLineSegment(sketch, "E393", {"start": v(-28.37, 12.46) * mm, "end": v(-32.2, 15.16) * mm});
            skLineSegment(sketch, "E394", {"start": v(-32.2, 15.16) * mm, "end": v(-36.04, 17.86) * mm});
            skLineSegment(sketch, "E395", {"start": v(-36.04, 17.86) * mm, "end": v(-40.14, 20.66) * mm});
            skLineSegment(sketch, "E396", {"start": v(-40.14, 20.66) * mm, "end": v(-44.76, 23.65) * mm});
            skLineSegment(sketch, "E397", {"start": v(-53.81, 4.48) * mm, "end": v(-53.63, 5.55) * mm});
            skLineSegment(sketch, "E398", {"start": v(-53.63, 5.55) * mm, "end": v(-53.43, 6.64) * mm});
            skLineSegment(sketch, "E399", {"start": v(-53.43, 6.64) * mm, "end": v(-53.07, 7.86) * mm});
            skLineSegment(sketch, "E400", {"start": v(-53.07, 7.86) * mm, "end": v(-52.39, 9.33) * mm});
            skLineSegment(sketch, "E401", {"start": v(-52.39, 9.33) * mm, "end": v(-50.68, 12.18) * mm});
            skLineSegment(sketch, "E402", {"start": v(-50.68, 12.18) * mm, "end": v(-43.98, 9.54) * mm});
            skLineSegment(sketch, "E403", {"start": v(-43.98, 9.54) * mm, "end": v(-40.46, 8.43) * mm});
            skLineSegment(sketch, "E404", {"start": v(-40.46, 8.43) * mm, "end": v(-37.62, 7.37) * mm});
            skLineSegment(sketch, "E405", {"start": v(-37.62, 7.37) * mm, "end": v(-35.23, 6.34) * mm});
            skLineSegment(sketch, "E406", {"start": v(-35.23, 6.34) * mm, "end": v(-33.07, 5.34) * mm});
            skLineSegment(sketch, "E407", {"start": v(-33.07, 5.34) * mm, "end": v(-33.25, 4.5) * mm});
            skLineSegment(sketch, "E408", {"start": v(-33.25, 4.5) * mm, "end": v(-33.47, 3.62) * mm});
            skLineSegment(sketch, "E409", {"start": v(-33.47, 3.62) * mm, "end": v(-33.84, 2.6) * mm});
            skLineSegment(sketch, "E410", {"start": v(-33.84, 2.6) * mm, "end": v(-34.43, 1.34) * mm});
            skLineSegment(sketch, "E411", {"start": v(-34.43, 1.34) * mm, "end": v(-53.81, 4.48) * mm});
            skSolve(sketch);
        }
        {
            var Q0;
            Q0=makeQuery(id+"F0.imprint","IMPRINT",FACE,{"disambiguationData":[TD([[makeQuery(id+"F0.imprint","IMPRINT",EDGE,{"derivedFrom":sQuery(id+"F0.wireOp",EDGE,"E130")}),-1.0]])]});
            var Q1;
            Q1=makeQuery(id+"F0.imprint","IMPRINT",FACE,{"disambiguationData":[TD([[makeQuery(id+"F0.imprint","IMPRINT",EDGE,{"derivedFrom":sQuery(id+"F0.wireOp",EDGE,"E115")}),-1.0]])]});
            var Q2;
            Q2=makeQuery(id+"F0.imprint","IMPRINT",FACE,{"disambiguationData":[TD([[makeQuery(id+"F0.imprint","IMPRINT",EDGE,{"derivedFrom":sQuery(id+"F0.wireOp",EDGE,"E397")}),-1.0]])]});
            var Q3;
            Q3=makeQuery(id+"F0.imprint","IMPRINT",FACE,{"disambiguationData":[TD([[makeQuery(id+"F0.imprint","IMPRINT",EDGE,{"derivedFrom":sQuery(id+"F0.wireOp",EDGE,"E379")}),1.0]])]});
            var Q4;
            Q4=makeQuery(id+"F0.imprint","IMPRINT",FACE,{"disambiguationData":[TD([[makeQuery(id+"F0.imprint","IMPRINT",EDGE,{"derivedFrom":sQuery(id+"F0.wireOp",EDGE,"E370")}),-1.0]])]});
            var Q5;
            Q5=makeQuery(id+"F0.imprint","IMPRINT",FACE,{"disambiguationData":[TD([[makeQuery(id+"F0.imprint","IMPRINT",EDGE,{"derivedFrom":sQuery(id+"F0.wireOp",EDGE,"E356")}),1.0]])]});
            var Q6;
            Q6=makeQuery(id+"F0.imprint","IMPRINT",FACE,{"disambiguationData":[TD([[makeQuery(id+"F0.imprint","IMPRINT",EDGE,{"derivedFrom":sQuery(id+"F0.wireOp",EDGE,"E347")}),-1.0]])]});
            var Q7;
            Q7=makeQuery(id+"F0.imprint","IMPRINT",FACE,{"disambiguationData":[TD([[makeQuery(id+"F0.imprint","IMPRINT",EDGE,{"derivedFrom":sQuery(id+"F0.wireOp",EDGE,"E333")}),-1.0]])]});
            var Q8;
            Q8=makeQuery(id+"F0.imprint","IMPRINT",FACE,{"disambiguationData":[TD([[makeQuery(id+"F0.imprint","IMPRINT",EDGE,{"derivedFrom":sQuery(id+"F0.wireOp",EDGE,"E312")}),-1.0]])]});
            var Q9;
            Q9=makeQuery(id+"F0.imprint","IMPRINT",FACE,{"disambiguationData":[TD([[makeQuery(id+"F0.imprint","IMPRINT",EDGE,{"derivedFrom":sQuery(id+"F0.wireOp",EDGE,"E0")}),-1.0]])]});
            extrude(context, id + "F1", {"entities" : qUnion([Q0, Q1, Q2, Q3, Q4, Q5, Q6, Q7, Q8, Q9]), "depth" : 22.86 * mm});
        }
        {
            var Q0;
            Q0=makeQuery(id+"F1.opExtrude","CAP_FACE",FACE,{"disambiguationData":[OSD([sQuery(id+"F0.wireOp",EDGE,"E130"),sQuery(id+"F0.wireOp",EDGE,"E131"),sQuery(id+"F0.wireOp",EDGE,"E132"),sQuery(id+"F0.wireOp",EDGE,"E133"),sQuery(id+"F0.wireOp",EDGE,"E134"),sQuery(id+"F0.wireOp",EDGE,"E135"),sQuery(id+"F0.wireOp",EDGE,"E136"),sQuery(id+"F0.wireOp",EDGE,"E137"),sQuery(id+"F0.wireOp",EDGE,"E138"),sQuery(id+"F0.wireOp",EDGE,"E139"),sQuery(id+"F0.wireOp",EDGE,"E140"),sQuery(id+"F0.wireOp",EDGE,"E141"),sQuery(id+"F0.wireOp",EDGE,"E142"),sQuery(id+"F0.wireOp",EDGE,"E143"),sQuery(id+"F0.wireOp",EDGE,"E144"),sQuery(id+"F0.wireOp",EDGE,"E145"),sQuery(id+"F0.wireOp",EDGE,"E146"),sQuery(id+"F0.wireOp",EDGE,"E147"),sQuery(id+"F0.wireOp",EDGE,"E148"),sQuery(id+"F0.wireOp",EDGE,"E149"),sQuery(id+"F0.wireOp",EDGE,"E150"),sQuery(id+"F0.wireOp",EDGE,"E151"),sQuery(id+"F0.wireOp",EDGE,"E152"),sQuery(id+"F0.wireOp",EDGE,"E153"),sQuery(id+"F0.wireOp",EDGE,"E154"),sQuery(id+"F0.wireOp",EDGE,"E155"),sQuery(id+"F0.wireOp",EDGE,"E156"),sQuery(id+"F0.wireOp",EDGE,"E157"),sQuery(id+"F0.wireOp",EDGE,"E158"),sQuery(id+"F0.wireOp",EDGE,"E159"),sQuery(id+"F0.wireOp",EDGE,"E160"),sQuery(id+"F0.wireOp",EDGE,"E161"),sQuery(id+"F0.wireOp",EDGE,"E162"),sQuery(id+"F0.wireOp",EDGE,"E163"),sQuery(id+"F0.wireOp",EDGE,"E164"),sQuery(id+"F0.wireOp",EDGE,"E165"),sQuery(id+"F0.wireOp",EDGE,"E166"),sQuery(id+"F0.wireOp",EDGE,"E167"),sQuery(id+"F0.wireOp",EDGE,"E168"),sQuery(id+"F0.wireOp",EDGE,"E169"),sQuery(id+"F0.wireOp",EDGE,"E170"),sQuery(id+"F0.wireOp",EDGE,"E171"),sQuery(id+"F0.wireOp",EDGE,"E172"),sQuery(id+"F0.wireOp",EDGE,"E173"),sQuery(id+"F0.wireOp",EDGE,"E174"),sQuery(id+"F0.wireOp",EDGE,"E175"),sQuery(id+"F0.wireOp",EDGE,"E176"),sQuery(id+"F0.wireOp",EDGE,"E177"),sQuery(id+"F0.wireOp",EDGE,"E178"),sQuery(id+"F0.wireOp",EDGE,"E179"),sQuery(id+"F0.wireOp",EDGE,"E180"),sQuery(id+"F0.wireOp",EDGE,"E181"),sQuery(id+"F0.wireOp",EDGE,"E182"),sQuery(id+"F0.wireOp",EDGE,"E183"),sQuery(id+"F0.wireOp",EDGE,"E184"),sQuery(id+"F0.wireOp",EDGE,"E185"),sQuery(id+"F0.wireOp",EDGE,"E186"),sQuery(id+"F0.wireOp",EDGE,"E187"),sQuery(id+"F0.wireOp",EDGE,"E188"),sQuery(id+"F0.wireOp",EDGE,"E189"),sQuery(id+"F0.wireOp",EDGE,"E190"),sQuery(id+"F0.wireOp",EDGE,"E191"),sQuery(id+"F0.wireOp",EDGE,"E192"),sQuery(id+"F0.wireOp",EDGE,"E193"),sQuery(id+"F0.wireOp",EDGE,"E194"),sQuery(id+"F0.wireOp",EDGE,"E195"),sQuery(id+"F0.wireOp",EDGE,"E196"),sQuery(id+"F0.wireOp",EDGE,"E197"),sQuery(id+"F0.wireOp",EDGE,"E198"),sQuery(id+"F0.wireOp",EDGE,"E199"),sQuery(id+"F0.wireOp",EDGE,"E200"),sQuery(id+"F0.wireOp",EDGE,"E201"),sQuery(id+"F0.wireOp",EDGE,"E202"),sQuery(id+"F0.wireOp",EDGE,"E203"),sQuery(id+"F0.wireOp",EDGE,"E204"),sQuery(id+"F0.wireOp",EDGE,"E205"),sQuery(id+"F0.wireOp",EDGE,"E206"),sQuery(id+"F0.wireOp",EDGE,"E207"),sQuery(id+"F0.wireOp",EDGE,"E208"),sQuery(id+"F0.wireOp",EDGE,"E209"),sQuery(id+"F0.wireOp",EDGE,"E210"),sQuery(id+"F0.wireOp",EDGE,"E211"),sQuery(id+"F0.wireOp",EDGE,"E212"),sQuery(id+"F0.wireOp",EDGE,"E213"),sQuery(id+"F0.wireOp",EDGE,"E214"),sQuery(id+"F0.wireOp",EDGE,"E215"),sQuery(id+"F0.wireOp",EDGE,"E216"),sQuery(id+"F0.wireOp",EDGE,"E217"),sQuery(id+"F0.wireOp",EDGE,"E218"),sQuery(id+"F0.wireOp",EDGE,"E219"),sQuery(id+"F0.wireOp",EDGE,"E220"),sQuery(id+"F0.wireOp",EDGE,"E221"),sQuery(id+"F0.wireOp",EDGE,"E222"),sQuery(id+"F0.wireOp",EDGE,"E223"),sQuery(id+"F0.wireOp",EDGE,"E224"),sQuery(id+"F0.wireOp",EDGE,"E225"),sQuery(id+"F0.wireOp",EDGE,"E226"),sQuery(id+"F0.wireOp",EDGE,"E227"),sQuery(id+"F0.wireOp",EDGE,"E228"),sQuery(id+"F0.wireOp",EDGE,"E229"),sQuery(id+"F0.wireOp",EDGE,"E230"),sQuery(id+"F0.wireOp",EDGE,"E231"),sQuery(id+"F0.wireOp",EDGE,"E232"),sQuery(id+"F0.wireOp",EDGE,"E233"),sQuery(id+"F0.wireOp",EDGE,"E234"),sQuery(id+"F0.wireOp",EDGE,"E235"),sQuery(id+"F0.wireOp",EDGE,"E236"),sQuery(id+"F0.wireOp",EDGE,"E237"),sQuery(id+"F0.wireOp",EDGE,"E238"),sQuery(id+"F0.wireOp",EDGE,"E239"),sQuery(id+"F0.wireOp",EDGE,"E240"),sQuery(id+"F0.wireOp",EDGE,"E241"),sQuery(id+"F0.wireOp",EDGE,"E242"),sQuery(id+"F0.wireOp",EDGE,"E243"),sQuery(id+"F0.wireOp",EDGE,"E244"),sQuery(id+"F0.wireOp",EDGE,"E245"),sQuery(id+"F0.wireOp",EDGE,"E246"),sQuery(id+"F0.wireOp",EDGE,"E247"),sQuery(id+"F0.wireOp",EDGE,"E248"),sQuery(id+"F0.wireOp",EDGE,"E249"),sQuery(id+"F0.wireOp",EDGE,"E250"),sQuery(id+"F0.wireOp",EDGE,"E251"),sQuery(id+"F0.wireOp",EDGE,"E252"),sQuery(id+"F0.wireOp",EDGE,"E253"),sQuery(id+"F0.wireOp",EDGE,"E254"),sQuery(id+"F0.wireOp",EDGE,"E255"),sQuery(id+"F0.wireOp",EDGE,"E256"),sQuery(id+"F0.wireOp",EDGE,"E257"),sQuery(id+"F0.wireOp",EDGE,"E258"),sQuery(id+"F0.wireOp",EDGE,"E259"),sQuery(id+"F0.wireOp",EDGE,"E260"),sQuery(id+"F0.wireOp",EDGE,"E261"),sQuery(id+"F0.wireOp",EDGE,"E262"),sQuery(id+"F0.wireOp",EDGE,"E263"),sQuery(id+"F0.wireOp",EDGE,"E264"),sQuery(id+"F0.wireOp",EDGE,"E265"),sQuery(id+"F0.wireOp",EDGE,"E266"),sQuery(id+"F0.wireOp",EDGE,"E267"),sQuery(id+"F0.wireOp",EDGE,"E268"),sQuery(id+"F0.wireOp",EDGE,"E269"),sQuery(id+"F0.wireOp",EDGE,"E270"),sQuery(id+"F0.wireOp",EDGE,"E271"),sQuery(id+"F0.wireOp",EDGE,"E272"),sQuery(id+"F0.wireOp",EDGE,"E273"),sQuery(id+"F0.wireOp",EDGE,"E274"),sQuery(id+"F0.wireOp",EDGE,"E275"),sQuery(id+"F0.wireOp",EDGE,"E276"),sQuery(id+"F0.wireOp",EDGE,"E277"),sQuery(id+"F0.wireOp",EDGE,"E278"),sQuery(id+"F0.wireOp",EDGE,"E279"),sQuery(id+"F0.wireOp",EDGE,"E280"),sQuery(id+"F0.wireOp",EDGE,"E281"),sQuery(id+"F0.wireOp",EDGE,"E282"),sQuery(id+"F0.wireOp",EDGE,"E283"),sQuery(id+"F0.wireOp",EDGE,"E284"),sQuery(id+"F0.wireOp",EDGE,"E285"),sQuery(id+"F0.wireOp",EDGE,"E286"),sQuery(id+"F0.wireOp",EDGE,"E287"),sQuery(id+"F0.wireOp",EDGE,"E288"),sQuery(id+"F0.wireOp",EDGE,"E289"),sQuery(id+"F0.wireOp",EDGE,"E290"),sQuery(id+"F0.wireOp",EDGE,"E291"),sQuery(id+"F0.wireOp",EDGE,"E292"),sQuery(id+"F0.wireOp",EDGE,"E293"),sQuery(id+"F0.wireOp",EDGE,"E294"),sQuery(id+"F0.wireOp",EDGE,"E295"),sQuery(id+"F0.wireOp",EDGE,"E296"),sQuery(id+"F0.wireOp",EDGE,"E297"),sQuery(id+"F0.wireOp",EDGE,"E298"),sQuery(id+"F0.wireOp",EDGE,"E299"),sQuery(id+"F0.wireOp",EDGE,"E300"),sQuery(id+"F0.wireOp",EDGE,"E301"),sQuery(id+"F0.wireOp",EDGE,"E302"),sQuery(id+"F0.wireOp",EDGE,"E303"),sQuery(id+"F0.wireOp",EDGE,"E304"),sQuery(id+"F0.wireOp",EDGE,"E305"),sQuery(id+"F0.wireOp",EDGE,"E306"),sQuery(id+"F0.wireOp",EDGE,"E307"),sQuery(id+"F0.wireOp",EDGE,"E308"),sQuery(id+"F0.wireOp",EDGE,"E309"),sQuery(id+"F0.wireOp",EDGE,"E310"),sQuery(id+"F0.wireOp",EDGE,"E311")])],"isStart":true});
            var sketch = newSketch(context, id + "F2", { "sketchPlane" : qUnion([Q0])});
            skLineSegment(sketch, "E412.0.0", {"start": v(-80.11, 82.47) * mm, "end": v(-81.82, 84.47) * mm});
            skLineSegment(sketch, "E412.0.1", {"start": v(-81.82, 84.47) * mm, "end": v(-78.24, 84) * mm});
            skLineSegment(sketch, "E412.0.2", {"start": v(-78.24, 84) * mm, "end": v(-74.68, 82.66) * mm});
            skLineSegment(sketch, "E412.0.3", {"start": v(-74.68, 82.66) * mm, "end": v(-71.24, 80.55) * mm});
            skLineSegment(sketch, "E412.0.4", {"start": v(-71.24, 80.55) * mm, "end": v(-68.03, 77.78) * mm});
            skLineSegment(sketch, "E412.0.5", {"start": v(-68.03, 77.78) * mm, "end": v(-65.13, 74.48) * mm});
            skLineSegment(sketch, "E412.0.6", {"start": v(-65.13, 74.48) * mm, "end": v(-62.66, 70.77) * mm});
            skLineSegment(sketch, "E412.0.7", {"start": v(-62.66, 70.77) * mm, "end": v(-60.7, 66.75) * mm});
            skLineSegment(sketch, "E412.0.8", {"start": v(-60.7, 66.75) * mm, "end": v(-59.36, 62.55) * mm});
            skLineSegment(sketch, "E412.0.9", {"start": v(-59.36, 62.55) * mm, "end": v(-58.28, 57.61) * mm});
            skLineSegment(sketch, "E412.0.10", {"start": v(-58.28, 57.61) * mm, "end": v(-57.38, 52.46) * mm});
            skLineSegment(sketch, "E412.0.11", {"start": v(-57.38, 52.46) * mm, "end": v(-56.78, 47.2) * mm});
            skLineSegment(sketch, "E412.0.12", {"start": v(-56.78, 47.2) * mm, "end": v(-56.58, 41.88) * mm});
            skLineSegment(sketch, "E412.0.13", {"start": v(-56.58, 41.88) * mm, "end": v(-56.84, 36.7) * mm});
            skLineSegment(sketch, "E412.0.14", {"start": v(-56.84, 36.7) * mm, "end": v(-57.47, 31.55) * mm});
            skLineSegment(sketch, "E412.0.15", {"start": v(-57.47, 31.55) * mm, "end": v(-58.37, 26.08) * mm});
            skLineSegment(sketch, "E412.0.16", {"start": v(-58.37, 26.08) * mm, "end": v(-59.47, 19.88) * mm});
            skLineSegment(sketch, "E412.0.17", {"start": v(-59.47, 19.88) * mm, "end": v(-59.8, 15.07) * mm});
            skLineSegment(sketch, "E412.0.18", {"start": v(-59.8, 15.07) * mm, "end": v(-60.2, 9.72) * mm});
            skLineSegment(sketch, "E412.0.19", {"start": v(-60.2, 9.72) * mm, "end": v(-60.33, 4.33) * mm});
            skLineSegment(sketch, "E412.0.20", {"start": v(-60.33, 4.33) * mm, "end": v(-59.9, -0.65) * mm});
            skLineSegment(sketch, "E412.0.21", {"start": v(-59.9, -0.65) * mm, "end": v(-59.22, -3.9) * mm});
            skLineSegment(sketch, "E412.0.22", {"start": v(-59.22, -3.9) * mm, "end": v(-58.17, -7.82) * mm});
            skLineSegment(sketch, "E412.0.23", {"start": v(-58.17, -7.82) * mm, "end": v(-57.17, -11.04) * mm});
            skLineSegment(sketch, "E412.0.24", {"start": v(-57.17, -11.04) * mm, "end": v(-56.4, -13.21) * mm});
            skLineSegment(sketch, "E412.0.25", {"start": v(-56.4, -13.21) * mm, "end": v(-56.1, -14) * mm});
            skLineSegment(sketch, "E412.0.26", {"start": v(-56.1, -14) * mm, "end": v(-55.32, -15.94) * mm});
            skLineSegment(sketch, "E412.0.27", {"start": v(-55.32, -15.94) * mm, "end": v(-53.9, -18.55) * mm});
            skLineSegment(sketch, "E412.0.28", {"start": v(-53.9, -18.55) * mm, "end": v(-51.92, -21.65) * mm});
            skLineSegment(sketch, "E412.0.29", {"start": v(-51.92, -21.65) * mm, "end": v(-49.52, -25.05) * mm});
            skLineSegment(sketch, "E412.0.30", {"start": v(-49.52, -25.05) * mm, "end": v(-46.82, -28.56) * mm});
            skLineSegment(sketch, "E412.0.31", {"start": v(-46.82, -28.56) * mm, "end": v(-43.9, -32) * mm});
            skLineSegment(sketch, "E412.0.32", {"start": v(-43.9, -32) * mm, "end": v(-40.92, -35.16) * mm});
            skLineSegment(sketch, "E412.0.33", {"start": v(-40.92, -35.16) * mm, "end": v(-37.97, -37.87) * mm});
            skLineSegment(sketch, "E412.0.34", {"start": v(-37.97, -37.87) * mm, "end": v(-32.85, -41.88) * mm});
            skLineSegment(sketch, "E412.0.35", {"start": v(-32.85, -41.88) * mm, "end": v(-27.92, -45.3) * mm});
            skLineSegment(sketch, "E412.0.36", {"start": v(-27.92, -45.3) * mm, "end": v(-23.16, -48.14) * mm});
            skLineSegment(sketch, "E412.0.37", {"start": v(-23.16, -48.14) * mm, "end": v(-18.58, -50.5) * mm});
            skLineSegment(sketch, "E412.0.38", {"start": v(-18.58, -50.5) * mm, "end": v(-14.18, -52.43) * mm});
            skLineSegment(sketch, "E412.0.39", {"start": v(-14.18, -52.43) * mm, "end": v(-9.96, -53.98) * mm});
            skLineSegment(sketch, "E412.0.40", {"start": v(-9.96, -53.98) * mm, "end": v(-5.93, -55.2) * mm});
            skLineSegment(sketch, "E412.0.41", {"start": v(-5.93, -55.2) * mm, "end": v(-2.08, -56.17) * mm});
            skLineSegment(sketch, "E412.0.42", {"start": v(-2.08, -56.17) * mm, "end": v(4.83, -57.42) * mm});
            skLineSegment(sketch, "E412.0.43", {"start": v(4.83, -57.42) * mm, "end": v(11.43, -57.98) * mm});
            skLineSegment(sketch, "E412.0.44", {"start": v(11.43, -57.98) * mm, "end": v(18.16, -57.96) * mm});
            skLineSegment(sketch, "E412.0.45", {"start": v(18.16, -57.96) * mm, "end": v(25.43, -57.47) * mm});
            skLineSegment(sketch, "E412.0.46", {"start": v(25.43, -57.47) * mm, "end": v(33.72, -56.27) * mm});
            skLineSegment(sketch, "E412.0.47", {"start": v(33.72, -56.27) * mm, "end": v(41.22, -54.4) * mm});
            skLineSegment(sketch, "E412.0.48", {"start": v(41.22, -54.4) * mm, "end": v(48.24, -52.04) * mm});
            skLineSegment(sketch, "E412.0.49", {"start": v(48.24, -52.04) * mm, "end": v(55.1, -49.38) * mm});
            skLineSegment(sketch, "E412.0.50", {"start": v(55.1, -49.38) * mm, "end": v(68.92, -79.74) * mm});
            skLineSegment(sketch, "E412.0.51", {"start": v(68.92, -79.74) * mm, "end": v(69.07, -79.97) * mm});
            skLineSegment(sketch, "E412.0.52", {"start": v(69.07, -79.97) * mm, "end": v(69.37, -80.54) * mm});
            skLineSegment(sketch, "E412.0.53", {"start": v(69.37, -80.54) * mm, "end": v(69.55, -81.28) * mm});
            skLineSegment(sketch, "E412.0.54", {"start": v(69.55, -81.28) * mm, "end": v(69.34, -82.02) * mm});
            skLineSegment(sketch, "E412.0.55", {"start": v(69.34, -82.02) * mm, "end": v(69.01, -82.39) * mm});
            skLineSegment(sketch, "E412.0.56", {"start": v(69.01, -82.39) * mm, "end": v(68.54, -82.77) * mm});
            skLineSegment(sketch, "E412.0.57", {"start": v(68.54, -82.77) * mm, "end": v(67.97, -83.16) * mm});
            skLineSegment(sketch, "E412.0.58", {"start": v(67.97, -83.16) * mm, "end": v(67.38, -83.52) * mm});
            skLineSegment(sketch, "E412.0.59", {"start": v(67.38, -83.52) * mm, "end": v(66.82, -83.84) * mm});
            skLineSegment(sketch, "E412.0.60", {"start": v(66.82, -83.84) * mm, "end": v(66.35, -84.09) * mm});
            skLineSegment(sketch, "E412.0.61", {"start": v(66.35, -84.09) * mm, "end": v(66.02, -84.26) * mm});
            skLineSegment(sketch, "E412.0.62", {"start": v(66.02, -84.26) * mm, "end": v(65.9, -84.32) * mm});
            skLineSegment(sketch, "E412.0.63", {"start": v(65.9, -84.32) * mm, "end": v(56.34, -88.2) * mm});
            skLineSegment(sketch, "E412.0.64", {"start": v(56.34, -88.2) * mm, "end": v(47.72, -91.15) * mm});
            skLineSegment(sketch, "E412.0.65", {"start": v(47.72, -91.15) * mm, "end": v(39.54, -93.1) * mm});
            skLineSegment(sketch, "E412.0.66", {"start": v(39.54, -93.1) * mm, "end": v(31.31, -93.97) * mm});
            skLineSegment(sketch, "E412.0.67", {"start": v(31.31, -93.97) * mm, "end": v(24.67, -94.08) * mm});
            skLineSegment(sketch, "E412.0.68", {"start": v(24.67, -94.08) * mm, "end": v(18.53, -93.92) * mm});
            skLineSegment(sketch, "E412.0.69", {"start": v(18.53, -93.92) * mm, "end": v(12.8, -93.51) * mm});
            skLineSegment(sketch, "E412.0.70", {"start": v(12.8, -93.51) * mm, "end": v(7.35, -92.87) * mm});
            skLineSegment(sketch, "E412.0.71", {"start": v(7.35, -92.87) * mm, "end": v(2.11, -92) * mm});
            skLineSegment(sketch, "E412.0.72", {"start": v(2.11, -92) * mm, "end": v(-3.03, -90.91) * mm});
            skLineSegment(sketch, "E412.0.73", {"start": v(-3.03, -90.91) * mm, "end": v(-8.18, -89.63) * mm});
            skLineSegment(sketch, "E412.0.74", {"start": v(-8.18, -89.63) * mm, "end": v(-13.43, -88.16) * mm});
            skLineSegment(sketch, "E412.0.75", {"start": v(-13.43, -88.16) * mm, "end": v(-17.96, -86.68) * mm});
            skLineSegment(sketch, "E412.0.76", {"start": v(-17.96, -86.68) * mm, "end": v(-22.57, -84.86) * mm});
            skLineSegment(sketch, "E412.0.77", {"start": v(-22.57, -84.86) * mm, "end": v(-27.23, -82.72) * mm});
            skLineSegment(sketch, "E412.0.78", {"start": v(-27.23, -82.72) * mm, "end": v(-31.9, -80.3) * mm});
            skLineSegment(sketch, "E412.0.79", {"start": v(-31.9, -80.3) * mm, "end": v(-36.55, -77.6) * mm});
            skLineSegment(sketch, "E412.0.80", {"start": v(-36.55, -77.6) * mm, "end": v(-41.12, -74.68) * mm});
            skLineSegment(sketch, "E412.0.81", {"start": v(-41.12, -74.68) * mm, "end": v(-45.6, -71.53) * mm});
            skLineSegment(sketch, "E412.0.82", {"start": v(-45.6, -71.53) * mm, "end": v(-49.92, -68.19) * mm});
            skLineSegment(sketch, "E412.0.83", {"start": v(-49.92, -68.19) * mm, "end": v(-54.06, -64.68) * mm});
            skLineSegment(sketch, "E412.0.84", {"start": v(-54.06, -64.68) * mm, "end": v(-57.99, -61.03) * mm});
            skLineSegment(sketch, "E412.0.85", {"start": v(-57.99, -61.03) * mm, "end": v(-61.65, -57.26) * mm});
            skLineSegment(sketch, "E412.0.86", {"start": v(-61.65, -57.26) * mm, "end": v(-65.02, -53.39) * mm});
            skLineSegment(sketch, "E412.0.87", {"start": v(-65.02, -53.39) * mm, "end": v(-68.05, -49.45) * mm});
            skLineSegment(sketch, "E412.0.88", {"start": v(-68.05, -49.45) * mm, "end": v(-70.71, -45.46) * mm});
            skLineSegment(sketch, "E412.0.89", {"start": v(-70.71, -45.46) * mm, "end": v(-72.96, -41.45) * mm});
            skLineSegment(sketch, "E412.0.90", {"start": v(-72.96, -41.45) * mm, "end": v(-74.76, -37.44) * mm});
            skLineSegment(sketch, "E412.0.91", {"start": v(-74.76, -37.44) * mm, "end": v(-77.55, -29.32) * mm});
            skLineSegment(sketch, "E412.0.92", {"start": v(-77.55, -29.32) * mm, "end": v(-79.67, -21.1) * mm});
            skLineSegment(sketch, "E412.0.93", {"start": v(-79.67, -21.1) * mm, "end": v(-81.12, -12.88) * mm});
            skLineSegment(sketch, "E412.0.94", {"start": v(-81.12, -12.88) * mm, "end": v(-81.9, -4.77) * mm});
            skLineSegment(sketch, "E412.0.95", {"start": v(-81.9, -4.77) * mm, "end": v(-82.04, 3.1) * mm});
            skLineSegment(sketch, "E412.0.96", {"start": v(-82.04, 3.1) * mm, "end": v(-81.52, 10.62) * mm});
            skLineSegment(sketch, "E412.0.97", {"start": v(-81.52, 10.62) * mm, "end": v(-80.35, 17.68) * mm});
            skLineSegment(sketch, "E412.0.98", {"start": v(-80.35, 17.68) * mm, "end": v(-78.54, 24.17) * mm});
            skLineSegment(sketch, "E412.0.99", {"start": v(-78.54, 24.17) * mm, "end": v(-75.57, 31.7) * mm});
            skLineSegment(sketch, "E412.0.100", {"start": v(-75.57, 31.7) * mm, "end": v(-73.35, 38.02) * mm});
            skLineSegment(sketch, "E412.0.101", {"start": v(-73.35, 38.02) * mm, "end": v(-71.78, 43.35) * mm});
            skLineSegment(sketch, "E412.0.102", {"start": v(-71.78, 43.35) * mm, "end": v(-70.77, 47.86) * mm});
            skLineSegment(sketch, "E412.0.103", {"start": v(-70.77, 47.86) * mm, "end": v(-70.22, 51.75) * mm});
            skLineSegment(sketch, "E412.0.104", {"start": v(-70.22, 51.75) * mm, "end": v(-70.03, 55.21) * mm});
            skLineSegment(sketch, "E412.0.105", {"start": v(-70.03, 55.21) * mm, "end": v(-70.11, 58.43) * mm});
            skLineSegment(sketch, "E412.0.106", {"start": v(-70.11, 58.43) * mm, "end": v(-70.36, 61.6) * mm});
            skLineSegment(sketch, "E412.0.107", {"start": v(-70.36, 61.6) * mm, "end": v(-71.28, 67.7) * mm});
            skLineSegment(sketch, "E412.0.108", {"start": v(-71.28, 67.7) * mm, "end": v(-72.61, 72.5) * mm});
            skLineSegment(sketch, "E412.0.109", {"start": v(-72.61, 72.5) * mm, "end": v(-74.2, 76.16) * mm});
            skLineSegment(sketch, "E412.0.110", {"start": v(-74.2, 76.16) * mm, "end": v(-75.88, 78.83) * mm});
            skLineSegment(sketch, "E412.0.111", {"start": v(-75.88, 78.83) * mm, "end": v(-77.48, 80.64) * mm});
            skLineSegment(sketch, "E412.0.112", {"start": v(-77.48, 80.64) * mm, "end": v(-78.83, 81.76) * mm});
            skLineSegment(sketch, "E412.0.113", {"start": v(-78.83, 81.76) * mm, "end": v(-79.76, 82.32) * mm});
            skLineSegment(sketch, "E412.0.114", {"start": v(-79.76, 82.32) * mm, "end": v(-80.11, 82.47) * mm});
            skLineSegment(sketch, "E413.0.0", {"start": v(-28.54, 76.85) * mm, "end": v(-28.63, 77.13) * mm});
            skLineSegment(sketch, "E413.0.1", {"start": v(-28.63, 77.13) * mm, "end": v(13.4, 66.65) * mm});
            skLineSegment(sketch, "E413.0.2", {"start": v(13.4, 66.65) * mm, "end": v(32.97, 79.9) * mm});
            skLineSegment(sketch, "E413.0.3", {"start": v(32.97, 79.9) * mm, "end": v(49.18, 89.1) * mm});
            skLineSegment(sketch, "E413.0.4", {"start": v(49.18, 89.1) * mm, "end": v(62.76, 94.08) * mm});
            skLineSegment(sketch, "E413.0.5", {"start": v(62.76, 94.08) * mm, "end": v(62.68, 93.66) * mm});
            skLineSegment(sketch, "E413.0.6", {"start": v(62.68, 93.66) * mm, "end": v(62.47, 92.48) * mm});
            skLineSegment(sketch, "E413.0.7", {"start": v(62.47, 92.48) * mm, "end": v(62.13, 90.64) * mm});
            skLineSegment(sketch, "E413.0.8", {"start": v(62.13, 90.64) * mm, "end": v(61.68, 88.25) * mm});
            skLineSegment(sketch, "E413.0.9", {"start": v(61.68, 88.25) * mm, "end": v(61.12, 85.4) * mm});
            skLineSegment(sketch, "E413.0.10", {"start": v(61.12, 85.4) * mm, "end": v(60.48, 82.18) * mm});
            skLineSegment(sketch, "E413.0.11", {"start": v(60.48, 82.18) * mm, "end": v(59.76, 78.71) * mm});
            skLineSegment(sketch, "E413.0.12", {"start": v(59.76, 78.71) * mm, "end": v(58.97, 75.1) * mm});
            skLineSegment(sketch, "E413.0.13", {"start": v(58.97, 75.1) * mm, "end": v(58.17, 70.86) * mm});
            skLineSegment(sketch, "E413.0.14", {"start": v(58.17, 70.86) * mm, "end": v(57.6, 66.74) * mm});
            skLineSegment(sketch, "E413.0.15", {"start": v(57.6, 66.74) * mm, "end": v(57.53, 66.17) * mm});
            skLineSegment(sketch, "E413.0.16", {"start": v(57.53, 66.17) * mm, "end": v(57.48, 65.83) * mm});
            skLineSegment(sketch, "E413.0.17", {"start": v(57.48, 65.83) * mm, "end": v(57.42, 65.36) * mm});
            skLineSegment(sketch, "E413.0.18", {"start": v(57.42, 65.36) * mm, "end": v(57.32, 64.36) * mm});
            skLineSegment(sketch, "E413.0.19", {"start": v(57.32, 64.36) * mm, "end": v(57.14, 62.89) * mm});
            skLineSegment(sketch, "E413.0.20", {"start": v(57.14, 62.89) * mm, "end": v(57.04, 62.2) * mm});
            skLineSegment(sketch, "E413.0.21", {"start": v(57.04, 62.2) * mm, "end": v(56.89, 61.42) * mm});
            skLineSegment(sketch, "E413.0.22", {"start": v(56.89, 61.42) * mm, "end": v(56.13, 57.56) * mm});
            skLineSegment(sketch, "E413.0.23", {"start": v(56.13, 57.56) * mm, "end": v(55.65, 53.17) * mm});
            skLineSegment(sketch, "E413.0.24", {"start": v(55.65, 53.17) * mm, "end": v(55.41, 48.56) * mm});
            skLineSegment(sketch, "E413.0.25", {"start": v(55.41, 48.56) * mm, "end": v(55.34, 44.07) * mm});
            skLineSegment(sketch, "E413.0.26", {"start": v(55.34, 44.07) * mm, "end": v(55.38, 40.01) * mm});
            skLineSegment(sketch, "E413.0.27", {"start": v(55.38, 40.01) * mm, "end": v(55.48, 36.71) * mm});
            skLineSegment(sketch, "E413.0.28", {"start": v(55.48, 36.71) * mm, "end": v(55.59, 34.5) * mm});
            skLineSegment(sketch, "E413.0.29", {"start": v(55.59, 34.5) * mm, "end": v(55.63, 33.69) * mm});
            skLineSegment(sketch, "E413.0.30", {"start": v(55.63, 33.69) * mm, "end": v(55.3, 33.72) * mm});
            skLineSegment(sketch, "E413.0.31", {"start": v(55.3, 33.72) * mm, "end": v(54.35, 33.8) * mm});
            skLineSegment(sketch, "E413.0.32", {"start": v(54.35, 33.8) * mm, "end": v(52.88, 33.85) * mm});
            skLineSegment(sketch, "E413.0.33", {"start": v(52.88, 33.85) * mm, "end": v(50.97, 33.83) * mm});
            skLineSegment(sketch, "E413.0.34", {"start": v(50.97, 33.83) * mm, "end": v(48.7, 33.7) * mm});
            skLineSegment(sketch, "E413.0.35", {"start": v(48.7, 33.7) * mm, "end": v(46.16, 33.4) * mm});
            skLineSegment(sketch, "E413.0.36", {"start": v(46.16, 33.4) * mm, "end": v(43.43, 32.87) * mm});
            skLineSegment(sketch, "E413.0.37", {"start": v(43.43, 32.87) * mm, "end": v(40.6, 32.08) * mm});
            skLineSegment(sketch, "E413.0.38", {"start": v(40.6, 32.08) * mm, "end": v(38.79, 31.33) * mm});
            skLineSegment(sketch, "E413.0.39", {"start": v(38.79, 31.33) * mm, "end": v(37.03, 30.37) * mm});
            skLineSegment(sketch, "E413.0.40", {"start": v(37.03, 30.37) * mm, "end": v(35.38, 29.3) * mm});
            skLineSegment(sketch, "E413.0.41", {"start": v(35.38, 29.3) * mm, "end": v(33.9, 28.2) * mm});
            skLineSegment(sketch, "E413.0.42", {"start": v(33.9, 28.2) * mm, "end": v(32.64, 27.17) * mm});
            skLineSegment(sketch, "E413.0.43", {"start": v(32.64, 27.17) * mm, "end": v(31.67, 26.32) * mm});
            skLineSegment(sketch, "E413.0.44", {"start": v(31.67, 26.32) * mm, "end": v(31.05, 25.74) * mm});
            skLineSegment(sketch, "E413.0.45", {"start": v(31.05, 25.74) * mm, "end": v(30.82, 25.52) * mm});
            skLineSegment(sketch, "E413.0.46", {"start": v(30.82, 25.52) * mm, "end": v(30.94, 25.36) * mm});
            skLineSegment(sketch, "E413.0.47", {"start": v(30.94, 25.36) * mm, "end": v(31.3, 24.9) * mm});
            skLineSegment(sketch, "E413.0.48", {"start": v(31.3, 24.9) * mm, "end": v(31.94, 24.2) * mm});
            skLineSegment(sketch, "E413.0.49", {"start": v(31.94, 24.2) * mm, "end": v(32.9, 23.33) * mm});
            skLineSegment(sketch, "E413.0.50", {"start": v(32.9, 23.33) * mm, "end": v(34.18, 22.33) * mm});
            skLineSegment(sketch, "E413.0.51", {"start": v(34.18, 22.33) * mm, "end": v(35.84, 21.26) * mm});
            skLineSegment(sketch, "E413.0.52", {"start": v(35.84, 21.26) * mm, "end": v(37.89, 20.17) * mm});
            skLineSegment(sketch, "E413.0.53", {"start": v(37.89, 20.17) * mm, "end": v(40.37, 19.13) * mm});
            skLineSegment(sketch, "E413.0.54", {"start": v(40.37, 19.13) * mm, "end": v(40.51, 19.1) * mm});
            skLineSegment(sketch, "E413.0.55", {"start": v(40.51, 19.1) * mm, "end": v(40.92, 19.06) * mm});
            skLineSegment(sketch, "E413.0.56", {"start": v(40.92, 19.06) * mm, "end": v(41.52, 18.99) * mm});
            skLineSegment(sketch, "E413.0.57", {"start": v(41.52, 18.99) * mm, "end": v(42.25, 18.91) * mm});
            skLineSegment(sketch, "E413.0.58", {"start": v(42.25, 18.91) * mm, "end": v(43.05, 18.83) * mm});
            skLineSegment(sketch, "E413.0.59", {"start": v(43.05, 18.83) * mm, "end": v(43.86, 18.77) * mm});
            skLineSegment(sketch, "E413.0.60", {"start": v(43.86, 18.77) * mm, "end": v(44.61, 18.72) * mm});
            skLineSegment(sketch, "E413.0.61", {"start": v(44.61, 18.72) * mm, "end": v(45.26, 18.71) * mm});
            skLineSegment(sketch, "E413.0.62", {"start": v(45.26, 18.71) * mm, "end": v(48.48, 19.05) * mm});
            skLineSegment(sketch, "E413.0.63", {"start": v(48.48, 19.05) * mm, "end": v(51.03, 19.73) * mm});
            skLineSegment(sketch, "E413.0.64", {"start": v(51.03, 19.73) * mm, "end": v(52.71, 20.39) * mm});
            skLineSegment(sketch, "E413.0.65", {"start": v(52.71, 20.39) * mm, "end": v(53.31, 20.69) * mm});
            skLineSegment(sketch, "E413.0.66", {"start": v(53.31, 20.69) * mm, "end": v(53.59, 20.86) * mm});
            skLineSegment(sketch, "E413.0.67", {"start": v(53.59, 20.86) * mm, "end": v(54.33, 21.38) * mm});
            skLineSegment(sketch, "E413.0.68", {"start": v(54.33, 21.38) * mm, "end": v(55.43, 22.24) * mm});
            skLineSegment(sketch, "E413.0.69", {"start": v(55.43, 22.24) * mm, "end": v(56.77, 23.46) * mm});
            skLineSegment(sketch, "E413.0.70", {"start": v(56.77, 23.46) * mm, "end": v(58.23, 25.03) * mm});
            skLineSegment(sketch, "E413.0.71", {"start": v(58.23, 25.03) * mm, "end": v(59.7, 26.95) * mm});
            skLineSegment(sketch, "E413.0.72", {"start": v(59.7, 26.95) * mm, "end": v(61.05, 29.23) * mm});
            skLineSegment(sketch, "E413.0.73", {"start": v(61.05, 29.23) * mm, "end": v(62.2, 31.86) * mm});
            skLineSegment(sketch, "E413.0.74", {"start": v(62.2, 31.86) * mm, "end": v(63, 34.68) * mm});
            skLineSegment(sketch, "E413.0.75", {"start": v(63, 34.68) * mm, "end": v(63.43, 37.34) * mm});
            skLineSegment(sketch, "E413.0.76", {"start": v(63.43, 37.34) * mm, "end": v(63.6, 39.79) * mm});
            skLineSegment(sketch, "E413.0.77", {"start": v(63.6, 39.79) * mm, "end": v(63.55, 41.94) * mm});
            skLineSegment(sketch, "E413.0.78", {"start": v(63.55, 41.94) * mm, "end": v(63.38, 43.74) * mm});
            skLineSegment(sketch, "E413.0.79", {"start": v(63.38, 43.74) * mm, "end": v(63.16, 45.1) * mm});
            skLineSegment(sketch, "E413.0.80", {"start": v(63.16, 45.1) * mm, "end": v(62.97, 45.98) * mm});
            skLineSegment(sketch, "E413.0.81", {"start": v(62.97, 45.98) * mm, "end": v(62.89, 46.29) * mm});
            skLineSegment(sketch, "E413.0.82", {"start": v(62.89, 46.29) * mm, "end": v(82.04, 49.81) * mm});
            skLineSegment(sketch, "E413.0.83", {"start": v(82.04, 49.81) * mm, "end": v(74.84, 39.93) * mm});
            skLineSegment(sketch, "E413.0.84", {"start": v(74.84, 39.93) * mm, "end": v(68.43, 29.1) * mm});
            skLineSegment(sketch, "E413.0.85", {"start": v(68.43, 29.1) * mm, "end": v(62.78, 17.36) * mm});
            skLineSegment(sketch, "E413.0.86", {"start": v(62.78, 17.36) * mm, "end": v(57.85, 4.76) * mm});
            skLineSegment(sketch, "E413.0.87", {"start": v(57.85, 4.76) * mm, "end": v(57.65, 4.43) * mm});
            skLineSegment(sketch, "E413.0.88", {"start": v(57.65, 4.43) * mm, "end": v(57.09, 3.54) * mm});
            skLineSegment(sketch, "E413.0.89", {"start": v(57.09, 3.54) * mm, "end": v(56.24, 2.21) * mm});
            skLineSegment(sketch, "E413.0.90", {"start": v(56.24, 2.21) * mm, "end": v(55.2, 0.6) * mm});
            skLineSegment(sketch, "E413.0.91", {"start": v(55.2, 0.6) * mm, "end": v(54, -1.15) * mm});
            skLineSegment(sketch, "E413.0.92", {"start": v(54, -1.15) * mm, "end": v(52.74, -2.92) * mm});
            skLineSegment(sketch, "E413.0.93", {"start": v(52.74, -2.92) * mm, "end": v(51.48, -4.57) * mm});
            skLineSegment(sketch, "E413.0.94", {"start": v(51.48, -4.57) * mm, "end": v(50.3, -5.94) * mm});
            skLineSegment(sketch, "E413.0.95", {"start": v(50.3, -5.94) * mm, "end": v(49.08, -7.15) * mm});
            skLineSegment(sketch, "E413.0.96", {"start": v(49.08, -7.15) * mm, "end": v(47.62, -8.44) * mm});
            skLineSegment(sketch, "E413.0.97", {"start": v(47.62, -8.44) * mm, "end": v(46.03, -9.75) * mm});
            skLineSegment(sketch, "E413.0.98", {"start": v(46.03, -9.75) * mm, "end": v(44.45, -11) * mm});
            skLineSegment(sketch, "E413.0.99", {"start": v(44.45, -11) * mm, "end": v(43, -12.1) * mm});
            skLineSegment(sketch, "E413.0.100", {"start": v(43, -12.1) * mm, "end": v(41.82, -12.99) * mm});
            skLineSegment(sketch, "E413.0.101", {"start": v(41.82, -12.99) * mm, "end": v(41.01, -13.57) * mm});
            skLineSegment(sketch, "E413.0.102", {"start": v(41.01, -13.57) * mm, "end": v(40.71, -13.79) * mm});
            skLineSegment(sketch, "E413.0.103", {"start": v(40.71, -13.79) * mm, "end": v(40.4, -13.97) * mm});
            skLineSegment(sketch, "E413.0.104", {"start": v(40.4, -13.97) * mm, "end": v(39.54, -14.48) * mm});
            skLineSegment(sketch, "E413.0.105", {"start": v(39.54, -14.48) * mm, "end": v(38.24, -15.23) * mm});
            skLineSegment(sketch, "E413.0.106", {"start": v(38.24, -15.23) * mm, "end": v(36.61, -16.13) * mm});
            skLineSegment(sketch, "E413.0.107", {"start": v(36.61, -16.13) * mm, "end": v(34.77, -17.1) * mm});
            skLineSegment(sketch, "E413.0.108", {"start": v(34.77, -17.1) * mm, "end": v(32.84, -18.06) * mm});
            skLineSegment(sketch, "E413.0.109", {"start": v(32.84, -18.06) * mm, "end": v(30.92, -18.92) * mm});
            skLineSegment(sketch, "E413.0.110", {"start": v(30.92, -18.92) * mm, "end": v(29.13, -19.6) * mm});
            skLineSegment(sketch, "E413.0.111", {"start": v(29.13, -19.6) * mm, "end": v(27.69, -20.01) * mm});
            skLineSegment(sketch, "E413.0.112", {"start": v(27.69, -20.01) * mm, "end": v(25.96, -20.43) * mm});
            skLineSegment(sketch, "E413.0.113", {"start": v(25.96, -20.43) * mm, "end": v(24.1, -20.82) * mm});
            skLineSegment(sketch, "E413.0.114", {"start": v(24.1, -20.82) * mm, "end": v(22.23, -21.19) * mm});
            skLineSegment(sketch, "E413.0.115", {"start": v(22.23, -21.19) * mm, "end": v(20.53, -21.5) * mm});
            skLineSegment(sketch, "E413.0.116", {"start": v(20.53, -21.5) * mm, "end": v(19.13, -21.74) * mm});
            skLineSegment(sketch, "E413.0.117", {"start": v(19.13, -21.74) * mm, "end": v(18.18, -21.9) * mm});
            skLineSegment(sketch, "E413.0.118", {"start": v(18.18, -21.9) * mm, "end": v(17.84, -21.95) * mm});
            skLineSegment(sketch, "E413.0.119", {"start": v(17.84, -21.95) * mm, "end": v(17.45, -21.96) * mm});
            skLineSegment(sketch, "E413.0.120", {"start": v(17.45, -21.96) * mm, "end": v(16.37, -21.98) * mm});
            skLineSegment(sketch, "E413.0.121", {"start": v(16.37, -21.98) * mm, "end": v(14.74, -22) * mm});
            skLineSegment(sketch, "E413.0.122", {"start": v(14.74, -22) * mm, "end": v(12.7, -22.02) * mm});
            skLineSegment(sketch, "E413.0.123", {"start": v(12.7, -22.02) * mm, "end": v(10.39, -22) * mm});
            skLineSegment(sketch, "E413.0.124", {"start": v(10.39, -22) * mm, "end": v(7.95, -21.93) * mm});
            skLineSegment(sketch, "E413.0.125", {"start": v(7.95, -21.93) * mm, "end": v(5.53, -21.8) * mm});
            skLineSegment(sketch, "E413.0.126", {"start": v(5.53, -21.8) * mm, "end": v(3.26, -21.57) * mm});
            skLineSegment(sketch, "E413.0.127", {"start": v(3.26, -21.57) * mm, "end": v(1.43, -21.14) * mm});
            skLineSegment(sketch, "E413.0.128", {"start": v(1.43, -21.14) * mm, "end": v(-0.57, -20.54) * mm});
            skLineSegment(sketch, "E413.0.129", {"start": v(-0.57, -20.54) * mm, "end": v(-2.63, -19.82) * mm});
            skLineSegment(sketch, "E413.0.130", {"start": v(-2.63, -19.82) * mm, "end": v(-4.6, -19.08) * mm});
            skLineSegment(sketch, "E413.0.131", {"start": v(-4.6, -19.08) * mm, "end": v(-6.36, -18.37) * mm});
            skLineSegment(sketch, "E413.0.132", {"start": v(-6.36, -18.37) * mm, "end": v(-7.79, -17.78) * mm});
            skLineSegment(sketch, "E413.0.133", {"start": v(-7.79, -17.78) * mm, "end": v(-8.73, -17.37) * mm});
            skLineSegment(sketch, "E413.0.134", {"start": v(-8.73, -17.37) * mm, "end": v(-9.08, -17.21) * mm});
            skLineSegment(sketch, "E413.0.135", {"start": v(-9.08, -17.21) * mm, "end": v(-9.64, -16.82) * mm});
            skLineSegment(sketch, "E413.0.136", {"start": v(-9.64, -16.82) * mm, "end": v(-11.17, -15.71) * mm});
            skLineSegment(sketch, "E413.0.137", {"start": v(-11.17, -15.71) * mm, "end": v(-13.4, -14.04) * mm});
            skLineSegment(sketch, "E413.0.138", {"start": v(-13.4, -14.04) * mm, "end": v(-16.07, -11.92) * mm});
            skLineSegment(sketch, "E413.0.139", {"start": v(-16.07, -11.92) * mm, "end": v(-18.95, -9.51) * mm});
            skLineSegment(sketch, "E413.0.140", {"start": v(-18.95, -9.51) * mm, "end": v(-21.77, -6.93) * mm});
            skLineSegment(sketch, "E413.0.141", {"start": v(-21.77, -6.93) * mm, "end": v(-24.28, -4.32) * mm});
            skLineSegment(sketch, "E413.0.142", {"start": v(-24.28, -4.32) * mm, "end": v(-26.22, -1.82) * mm});
            skLineSegment(sketch, "E413.0.143", {"start": v(-26.22, -1.82) * mm, "end": v(-27.95, 1.1) * mm});
            skLineSegment(sketch, "E413.0.144", {"start": v(-27.95, 1.1) * mm, "end": v(-29.6, 4.42) * mm});
            skLineSegment(sketch, "E413.0.145", {"start": v(-29.6, 4.42) * mm, "end": v(-31.06, 7.95) * mm});
            skLineSegment(sketch, "E413.0.146", {"start": v(-31.06, 7.95) * mm, "end": v(-32.25, 11.5) * mm});
            skLineSegment(sketch, "E413.0.147", {"start": v(-32.25, 11.5) * mm, "end": v(-32.78, 13.95) * mm});
            skLineSegment(sketch, "E413.0.148", {"start": v(-32.78, 13.95) * mm, "end": v(-33.16, 16.7) * mm});
            skLineSegment(sketch, "E413.0.149", {"start": v(-33.16, 16.7) * mm, "end": v(-33.4, 18.95) * mm});
            skLineSegment(sketch, "E413.0.150", {"start": v(-33.4, 18.95) * mm, "end": v(-33.47, 19.88) * mm});
            skLineSegment(sketch, "E413.0.151", {"start": v(-33.47, 19.88) * mm, "end": v(-33.44, 20.32) * mm});
            skLineSegment(sketch, "E413.0.152", {"start": v(-33.44, 20.32) * mm, "end": v(-33.35, 21.55) * mm});
            skLineSegment(sketch, "E413.0.153", {"start": v(-33.35, 21.55) * mm, "end": v(-33.2, 23.4) * mm});
            skLineSegment(sketch, "E413.0.154", {"start": v(-33.2, 23.4) * mm, "end": v(-32.95, 25.69) * mm});
            skLineSegment(sketch, "E413.0.155", {"start": v(-32.95, 25.69) * mm, "end": v(-32.63, 28.27) * mm});
            skLineSegment(sketch, "E413.0.156", {"start": v(-32.63, 28.27) * mm, "end": v(-32.2, 30.97) * mm});
            skLineSegment(sketch, "E413.0.157", {"start": v(-32.2, 30.97) * mm, "end": v(-31.67, 33.63) * mm});
            skLineSegment(sketch, "E413.0.158", {"start": v(-31.67, 33.63) * mm, "end": v(-31.02, 36.08) * mm});
            skLineSegment(sketch, "E413.0.159", {"start": v(-31.02, 36.08) * mm, "end": v(-30.71, 37.4) * mm});
            skLineSegment(sketch, "E413.0.160", {"start": v(-30.71, 37.4) * mm, "end": v(-30.25, 39.11) * mm});
            skLineSegment(sketch, "E413.0.161", {"start": v(-30.25, 39.11) * mm, "end": v(-29.69, 41.13) * mm});
            skLineSegment(sketch, "E413.0.162", {"start": v(-29.69, 41.13) * mm, "end": v(-29.06, 43.3) * mm});
            skLineSegment(sketch, "E413.0.163", {"start": v(-29.06, 43.3) * mm, "end": v(-28.42, 45.53) * mm});
            skLineSegment(sketch, "E413.0.164", {"start": v(-28.42, 45.53) * mm, "end": v(-27.8, 47.67) * mm});
            skLineSegment(sketch, "E413.0.165", {"start": v(-27.8, 47.67) * mm, "end": v(-27.25, 49.6) * mm});
            skLineSegment(sketch, "E413.0.166", {"start": v(-27.25, 49.6) * mm, "end": v(-26.82, 51.22) * mm});
            skLineSegment(sketch, "E413.0.167", {"start": v(-26.82, 51.22) * mm, "end": v(-26.19, 54.03) * mm});
            skLineSegment(sketch, "E413.0.168", {"start": v(-26.19, 54.03) * mm, "end": v(-25.75, 56.56) * mm});
            skLineSegment(sketch, "E413.0.169", {"start": v(-25.75, 56.56) * mm, "end": v(-25.5, 58.38) * mm});
            skLineSegment(sketch, "E413.0.170", {"start": v(-25.5, 58.38) * mm, "end": v(-25.4, 59.09) * mm});
            skLineSegment(sketch, "E413.0.171", {"start": v(-25.4, 59.09) * mm, "end": v(-25.4, 59.98) * mm});
            skLineSegment(sketch, "E413.0.172", {"start": v(-25.4, 59.98) * mm, "end": v(-25.44, 62.18) * mm});
            skLineSegment(sketch, "E413.0.173", {"start": v(-25.44, 62.18) * mm, "end": v(-25.58, 64.97) * mm});
            skLineSegment(sketch, "E413.0.174", {"start": v(-25.58, 64.97) * mm, "end": v(-25.9, 67.6) * mm});
            skLineSegment(sketch, "E413.0.175", {"start": v(-25.9, 67.6) * mm, "end": v(-26.18, 68.9) * mm});
            skLineSegment(sketch, "E413.0.176", {"start": v(-26.18, 68.9) * mm, "end": v(-26.57, 70.4) * mm});
            skLineSegment(sketch, "E413.0.177", {"start": v(-26.57, 70.4) * mm, "end": v(-27.02, 71.97) * mm});
            skLineSegment(sketch, "E413.0.178", {"start": v(-27.02, 71.97) * mm, "end": v(-27.48, 73.52) * mm});
            skLineSegment(sketch, "E413.0.179", {"start": v(-27.48, 73.52) * mm, "end": v(-27.92, 74.93) * mm});
            skLineSegment(sketch, "E413.0.180", {"start": v(-27.92, 74.93) * mm, "end": v(-28.29, 76.07) * mm});
            skLineSegment(sketch, "E413.0.181", {"start": v(-28.29, 76.07) * mm, "end": v(-28.54, 76.85) * mm});
            skLineSegment(sketch, "E414.0.0", {"start": v(-55.07, 19.51) * mm, "end": v(-54.53, 25.24) * mm});
            skLineSegment(sketch, "E414.0.1", {"start": v(-54.53, 25.24) * mm, "end": v(-53.5, 21.42) * mm});
            skLineSegment(sketch, "E414.0.2", {"start": v(-53.5, 21.42) * mm, "end": v(-52.26, 17.9) * mm});
            skLineSegment(sketch, "E414.0.3", {"start": v(-52.26, 17.9) * mm, "end": v(-50.75, 14.73) * mm});
            skLineSegment(sketch, "E414.0.4", {"start": v(-50.75, 14.73) * mm, "end": v(-48.95, 11.97) * mm});
            skLineSegment(sketch, "E414.0.5", {"start": v(-48.95, 11.97) * mm, "end": v(-46.8, 9.68) * mm});
            skLineSegment(sketch, "E414.0.6", {"start": v(-46.8, 9.68) * mm, "end": v(-44.26, 7.92) * mm});
            skLineSegment(sketch, "E414.0.7", {"start": v(-44.26, 7.92) * mm, "end": v(-41.3, 6.74) * mm});
            skLineSegment(sketch, "E414.0.8", {"start": v(-41.3, 6.74) * mm, "end": v(-37.85, 6.21) * mm});
            skLineSegment(sketch, "E414.0.9", {"start": v(-37.85, 6.21) * mm, "end": v(-37.13, 2.22) * mm});
            skLineSegment(sketch, "E414.0.10", {"start": v(-37.13, 2.22) * mm, "end": v(-53.88, -0.13) * mm});
            skLineSegment(sketch, "E414.0.11", {"start": v(-53.88, -0.13) * mm, "end": v(-54.81, 0.87) * mm});
            skLineSegment(sketch, "E414.0.12", {"start": v(-54.81, 0.87) * mm, "end": v(-55.65, 7.67) * mm});
            skLineSegment(sketch, "E414.0.13", {"start": v(-55.65, 7.67) * mm, "end": v(-55.59, 13.77) * mm});
            skLineSegment(sketch, "E414.0.14", {"start": v(-55.59, 13.77) * mm, "end": v(-55.07, 19.51) * mm});
            skLineSegment(sketch, "E415.0", {"start": v(-34.43, -1.34) * mm, "end": v(-53.81, -4.48) * mm});
            skLineSegment(sketch, "E416.0.0", {"start": v(-53.63, -5.55) * mm, "end": v(-53.81, -4.48) * mm});
            skLineSegment(sketch, "E416.0.1", {"start": v(-53.81, -4.48) * mm, "end": v(-34.43, -1.34) * mm});
            skLineSegment(sketch, "E416.0.2", {"start": v(-34.43, -1.34) * mm, "end": v(-33.84, -2.6) * mm});
            skLineSegment(sketch, "E416.0.3", {"start": v(-33.84, -2.6) * mm, "end": v(-33.47, -3.62) * mm});
            skLineSegment(sketch, "E416.0.4", {"start": v(-33.47, -3.62) * mm, "end": v(-33.25, -4.5) * mm});
            skLineSegment(sketch, "E416.0.5", {"start": v(-33.25, -4.5) * mm, "end": v(-33.07, -5.34) * mm});
            skLineSegment(sketch, "E416.0.6", {"start": v(-33.07, -5.34) * mm, "end": v(-35.23, -6.34) * mm});
            skLineSegment(sketch, "E416.0.7", {"start": v(-35.23, -6.34) * mm, "end": v(-37.62, -7.37) * mm});
            skLineSegment(sketch, "E416.0.8", {"start": v(-37.62, -7.37) * mm, "end": v(-40.46, -8.43) * mm});
            skLineSegment(sketch, "E416.0.9", {"start": v(-40.46, -8.43) * mm, "end": v(-43.98, -9.54) * mm});
            skLineSegment(sketch, "E416.0.10", {"start": v(-43.98, -9.54) * mm, "end": v(-50.68, -12.18) * mm});
            skLineSegment(sketch, "E416.0.11", {"start": v(-50.68, -12.18) * mm, "end": v(-52.39, -9.33) * mm});
            skLineSegment(sketch, "E416.0.12", {"start": v(-52.39, -9.33) * mm, "end": v(-53.07, -7.86) * mm});
            skLineSegment(sketch, "E416.0.13", {"start": v(-53.07, -7.86) * mm, "end": v(-53.43, -6.64) * mm});
            skLineSegment(sketch, "E416.0.14", {"start": v(-53.43, -6.64) * mm, "end": v(-53.63, -5.55) * mm});
            skLineSegment(sketch, "E417.0.0", {"start": v(-40.14, -20.66) * mm, "end": v(-44.76, -23.65) * mm});
            skLineSegment(sketch, "E417.0.1", {"start": v(-44.76, -23.65) * mm, "end": v(-47.47, -20.02) * mm});
            skLineSegment(sketch, "E417.0.2", {"start": v(-47.47, -20.02) * mm, "end": v(-49.04, -15.95) * mm});
            skLineSegment(sketch, "E417.0.3", {"start": v(-49.04, -15.95) * mm, "end": v(-44.05, -13.7) * mm});
            skLineSegment(sketch, "E417.0.4", {"start": v(-44.05, -13.7) * mm, "end": v(-39.14, -11.5) * mm});
            skLineSegment(sketch, "E417.0.5", {"start": v(-39.14, -11.5) * mm, "end": v(-34.6, -9.52) * mm});
            skLineSegment(sketch, "E417.0.6", {"start": v(-34.6, -9.52) * mm, "end": v(-30.72, -7.97) * mm});
            skLineSegment(sketch, "E417.0.7", {"start": v(-30.72, -7.97) * mm, "end": v(-30.5, -8.38) * mm});
            skLineSegment(sketch, "E417.0.8", {"start": v(-30.5, -8.38) * mm, "end": v(-30.3, -8.74) * mm});
            skLineSegment(sketch, "E417.0.9", {"start": v(-30.3, -8.74) * mm, "end": v(-30.1, -9.1) * mm});
            skLineSegment(sketch, "E417.0.10", {"start": v(-30.1, -9.1) * mm, "end": v(-29.87, -9.5) * mm});
            skLineSegment(sketch, "E417.0.11", {"start": v(-29.87, -9.5) * mm, "end": v(-29.6, -10) * mm});
            skLineSegment(sketch, "E417.0.12", {"start": v(-29.6, -10) * mm, "end": v(-29.28, -10.62) * mm});
            skLineSegment(sketch, "E417.0.13", {"start": v(-29.28, -10.62) * mm, "end": v(-28.88, -11.43) * mm});
            skLineSegment(sketch, "E417.0.14", {"start": v(-28.88, -11.43) * mm, "end": v(-28.37, -12.46) * mm});
            skLineSegment(sketch, "E417.0.15", {"start": v(-28.37, -12.46) * mm, "end": v(-32.2, -15.16) * mm});
            skLineSegment(sketch, "E417.0.16", {"start": v(-32.2, -15.16) * mm, "end": v(-36.04, -17.86) * mm});
            skLineSegment(sketch, "E417.0.17", {"start": v(-36.04, -17.86) * mm, "end": v(-40.14, -20.66) * mm});
            skLineSegment(sketch, "E418.0.0", {"start": v(-40.56, -28.53) * mm, "end": v(-41.7, -26.72) * mm});
            skLineSegment(sketch, "E418.0.1", {"start": v(-41.7, -26.72) * mm, "end": v(-24.1, -14.53) * mm});
            skLineSegment(sketch, "E418.0.2", {"start": v(-24.1, -14.53) * mm, "end": v(-22.8, -15.81) * mm});
            skLineSegment(sketch, "E418.0.3", {"start": v(-22.8, -15.81) * mm, "end": v(-21.7, -16.85) * mm});
            skLineSegment(sketch, "E418.0.4", {"start": v(-21.7, -16.85) * mm, "end": v(-21.03, -18.02) * mm});
            skLineSegment(sketch, "E418.0.5", {"start": v(-21.03, -18.02) * mm, "end": v(-35.57, -33.63) * mm});
            skLineSegment(sketch, "E418.0.6", {"start": v(-35.57, -33.63) * mm, "end": v(-37.65, -32.03) * mm});
            skLineSegment(sketch, "E418.0.7", {"start": v(-37.65, -32.03) * mm, "end": v(-39.26, -30.31) * mm});
            skLineSegment(sketch, "E418.0.8", {"start": v(-39.26, -30.31) * mm, "end": v(-40.56, -28.53) * mm});
            skLineSegment(sketch, "E419.0.0", {"start": v(-22.1, -35.82) * mm, "end": v(-25.02, -41.33) * mm});
            skLineSegment(sketch, "E419.0.1", {"start": v(-25.02, -41.33) * mm, "end": v(-27.64, -40.71) * mm});
            skLineSegment(sketch, "E419.0.2", {"start": v(-27.64, -40.71) * mm, "end": v(-29.63, -39.53) * mm});
            skLineSegment(sketch, "E419.0.3", {"start": v(-29.63, -39.53) * mm, "end": v(-31.21, -37.96) * mm});
            skLineSegment(sketch, "E419.0.4", {"start": v(-31.21, -37.96) * mm, "end": v(-32.57, -36.2) * mm});
            skLineSegment(sketch, "E419.0.5", {"start": v(-32.57, -36.2) * mm, "end": v(-19.25, -20.3) * mm});
            skLineSegment(sketch, "E419.0.6", {"start": v(-19.25, -20.3) * mm, "end": v(-18.54, -20.2) * mm});
            skLineSegment(sketch, "E419.0.7", {"start": v(-18.54, -20.2) * mm, "end": v(-18.02, -20.17) * mm});
            skLineSegment(sketch, "E419.0.8", {"start": v(-18.02, -20.17) * mm, "end": v(-17.6, -20.16) * mm});
            skLineSegment(sketch, "E419.0.9", {"start": v(-17.6, -20.16) * mm, "end": v(-17.18, -20.16) * mm});
            skLineSegment(sketch, "E419.0.10", {"start": v(-17.18, -20.16) * mm, "end": v(-13.9, -22.51) * mm});
            skLineSegment(sketch, "E419.0.11", {"start": v(-13.9, -22.51) * mm, "end": v(-16.63, -26.88) * mm});
            skLineSegment(sketch, "E419.0.12", {"start": v(-16.63, -26.88) * mm, "end": v(-19.33, -31.16) * mm});
            skLineSegment(sketch, "E419.0.13", {"start": v(-19.33, -31.16) * mm, "end": v(-22.1, -35.82) * mm});
            skLineSegment(sketch, "E420.0.0", {"start": v(-9.1, -37.44) * mm, "end": v(-12.47, -47.81) * mm});
            skLineSegment(sketch, "E420.0.1", {"start": v(-12.47, -47.81) * mm, "end": v(-16.68, -46.24) * mm});
            skLineSegment(sketch, "E420.0.2", {"start": v(-16.68, -46.24) * mm, "end": v(-21.03, -43.82) * mm});
            skLineSegment(sketch, "E420.0.3", {"start": v(-21.03, -43.82) * mm, "end": v(-18.71, -38.44) * mm});
            skLineSegment(sketch, "E420.0.4", {"start": v(-18.71, -38.44) * mm, "end": v(-16.29, -33.35) * mm});
            skLineSegment(sketch, "E420.0.5", {"start": v(-16.29, -33.35) * mm, "end": v(-13.72, -28.65) * mm});
            skLineSegment(sketch, "E420.0.6", {"start": v(-13.72, -28.65) * mm, "end": v(-10.98, -24.44) * mm});
            skLineSegment(sketch, "E420.0.7", {"start": v(-10.98, -24.44) * mm, "end": v(-5.7, -26.57) * mm});
            skLineSegment(sketch, "E420.0.8", {"start": v(-5.7, -26.57) * mm, "end": v(-9.1, -37.44) * mm});
            skLineSegment(sketch, "E421.0.0", {"start": v(-5.31, -50.04) * mm, "end": v(-8.2, -49.45) * mm});
            skLineSegment(sketch, "E421.0.1", {"start": v(-8.2, -49.45) * mm, "end": v(-7.14, -43.38) * mm});
            skLineSegment(sketch, "E421.0.2", {"start": v(-7.14, -43.38) * mm, "end": v(-5.84, -37.85) * mm});
            skLineSegment(sketch, "E421.0.3", {"start": v(-5.84, -37.85) * mm, "end": v(-4.37, -32.7) * mm});
            skLineSegment(sketch, "E421.0.4", {"start": v(-4.37, -32.7) * mm, "end": v(-2.78, -27.79) * mm});
            skLineSegment(sketch, "E421.0.5", {"start": v(-2.78, -27.79) * mm, "end": v(2.78, -28.57) * mm});
            skLineSegment(sketch, "E421.0.6", {"start": v(2.78, -28.57) * mm, "end": v(2.28, -51.1) * mm});
            skLineSegment(sketch, "E421.0.7", {"start": v(2.28, -51.1) * mm, "end": v(2.18, -51.1) * mm});
            skLineSegment(sketch, "E421.0.8", {"start": v(2.18, -51.1) * mm, "end": v(1.83, -51.09) * mm});
            skLineSegment(sketch, "E421.0.9", {"start": v(1.83, -51.09) * mm, "end": v(1.2, -51.04) * mm});
            skLineSegment(sketch, "E421.0.10", {"start": v(1.2, -51.04) * mm, "end": v(0.22, -50.94) * mm});
            skLineSegment(sketch, "E421.0.11", {"start": v(0.22, -50.94) * mm, "end": v(-1.15, -50.75) * mm});
            skLineSegment(sketch, "E421.0.12", {"start": v(-1.15, -50.75) * mm, "end": v(-2.98, -50.46) * mm});
            skLineSegment(sketch, "E421.0.13", {"start": v(-2.98, -50.46) * mm, "end": v(-5.31, -50.04) * mm});
            skLineSegment(sketch, "E422.0.0", {"start": v(6.77, -34.65) * mm, "end": v(6.91, -29.14) * mm});
            skLineSegment(sketch, "E422.0.1", {"start": v(6.91, -29.14) * mm, "end": v(9.9, -29) * mm});
            skLineSegment(sketch, "E422.0.2", {"start": v(9.9, -29) * mm, "end": v(10.27, -31.41) * mm});
            skLineSegment(sketch, "E422.0.3", {"start": v(10.27, -31.41) * mm, "end": v(11.18, -34.3) * mm});
            skLineSegment(sketch, "E422.0.4", {"start": v(11.18, -34.3) * mm, "end": v(12.77, -37.42) * mm});
            skLineSegment(sketch, "E422.0.5", {"start": v(12.77, -37.42) * mm, "end": v(15.2, -40.57) * mm});
            skLineSegment(sketch, "E422.0.6", {"start": v(15.2, -40.57) * mm, "end": v(18.6, -43.53) * mm});
            skLineSegment(sketch, "E422.0.7", {"start": v(18.6, -43.53) * mm, "end": v(23.1, -46.07) * mm});
            skLineSegment(sketch, "E422.0.8", {"start": v(23.1, -46.07) * mm, "end": v(28.88, -47.98) * mm});
            skLineSegment(sketch, "E422.0.9", {"start": v(28.88, -47.98) * mm, "end": v(36.06, -49.02) * mm});
            skLineSegment(sketch, "E422.0.10", {"start": v(36.06, -49.02) * mm, "end": v(33.27, -49.88) * mm});
            skLineSegment(sketch, "E422.0.11", {"start": v(33.27, -49.88) * mm, "end": v(30.45, -50.72) * mm});
            skLineSegment(sketch, "E422.0.12", {"start": v(30.45, -50.72) * mm, "end": v(27.5, -51.48) * mm});
            skLineSegment(sketch, "E422.0.13", {"start": v(27.5, -51.48) * mm, "end": v(24.31, -52.1) * mm});
            skLineSegment(sketch, "E422.0.14", {"start": v(24.31, -52.1) * mm, "end": v(20.8, -52.53) * mm});
            skLineSegment(sketch, "E422.0.15", {"start": v(20.8, -52.53) * mm, "end": v(16.87, -52.7) * mm});
            skLineSegment(sketch, "E422.0.16", {"start": v(16.87, -52.7) * mm, "end": v(12.42, -52.54) * mm});
            skLineSegment(sketch, "E422.0.17", {"start": v(12.42, -52.54) * mm, "end": v(7.34, -52.02) * mm});
            skLineSegment(sketch, "E422.0.18", {"start": v(7.34, -52.02) * mm, "end": v(6.86, -46) * mm});
            skLineSegment(sketch, "E422.0.19", {"start": v(6.86, -46) * mm, "end": v(6.71, -40.24) * mm});
            skLineSegment(sketch, "E422.0.20", {"start": v(6.71, -40.24) * mm, "end": v(6.77, -34.65) * mm});
            skLineSegment(sketch, "E423.bottom", {"start": v(-101.6, -114.3) * mm, "end": v(101.6, -114.3) * mm});
            skLineSegment(sketch, "E423.top", {"start": v(-101.6, 107.95) * mm, "end": v(101.6, 107.95) * mm});
            skLineSegment(sketch, "E423.left", {"start": v(-101.6, -114.3) * mm, "end": v(-101.6, 107.95) * mm});
            skLineSegment(sketch, "E423.right", {"start": v(101.6, -114.3) * mm, "end": v(101.6, 107.95) * mm});
            skCircle(sketch, "E424", {"center": v(-93.47, -106.17) * mm, "radius": 5.72 * mm});
            skSolve(sketch);
        }
        {
            var Q0;
            Q0=makeQuery(id+"F2.imprint","IMPRINT",FACE,{"disambiguationData":[TD([[makeQuery(id+"F2.imprint","IMPRINT",EDGE,{"derivedFrom":sQuery(id+"F2.wireOp",EDGE,"E412.0.0")}),1.0]])]});
            extrude(context, id + "F3", {"entities" : qUnion([Q0]), "oppositeDirection" : true, "depth" : 11.6 * mm});
        }
        {
            var Q0;
            Q0=makeQuery(id+"F3.opExtrude","SWEPT_EDGE",EDGE,{"disambiguationData":[OSD([sQuery(id+"F2.wireOp",EDGE,"E423.bottom"),sQuery(id+"F2.wireOp",EDGE,"E423.left")])]});
            var Q1;
            Q1=makeQuery(id+"F3.opExtrude","SWEPT_EDGE",EDGE,{"disambiguationData":[OSD([sQuery(id+"F2.wireOp",EDGE,"E423.top"),sQuery(id+"F2.wireOp",EDGE,"E423.left")])]});
            var Q2;
            Q2=makeQuery(id+"F3.opExtrude","SWEPT_EDGE",EDGE,{"disambiguationData":[OSD([sQuery(id+"F2.wireOp",EDGE,"E423.top"),sQuery(id+"F2.wireOp",EDGE,"E423.right")])]});
            var Q3;
            Q3=makeQuery(id+"F3.opExtrude","SWEPT_EDGE",EDGE,{"disambiguationData":[OSD([sQuery(id+"F2.wireOp",EDGE,"E423.bottom"),sQuery(id+"F2.wireOp",EDGE,"E423.right")])]});
            fillet(context, id + "F4", {"entities" : qUnion([Q0, Q1, Q2, Q3]), "radius" : 5.08 * mm, "tangentPropagation" : true, "allowEdgeOverflow" : false});
        }
        {
            var Q0;
            Q0=makeQuery(id+"F3.opExtrude","CAP_EDGE",EDGE,{"disambiguationData":[OSD([sQuery(id+"F2.wireOp",EDGE,"E423.right")])],"isStart":false});
            var Q1;
            Q1=makeQuery(id+"F3.opExtrude","CAP_EDGE",EDGE,{"disambiguationData":[OSD([sQuery(id+"F2.wireOp",EDGE,"E424")])],"isStart":false});
            var Q2;
            Q2=makeQuery(id+"F3.opExtrude","CAP_EDGE",EDGE,{"disambiguationData":[OSD([sQuery(id+"F2.wireOp",EDGE,"E424")])],"isStart":true});
            chamfer(context, id + "F5", {"entities" : qUnion([Q0, Q1, Q2]), "width" : 2.03 * mm, "tangentPropagation" : true});
        }
    });
